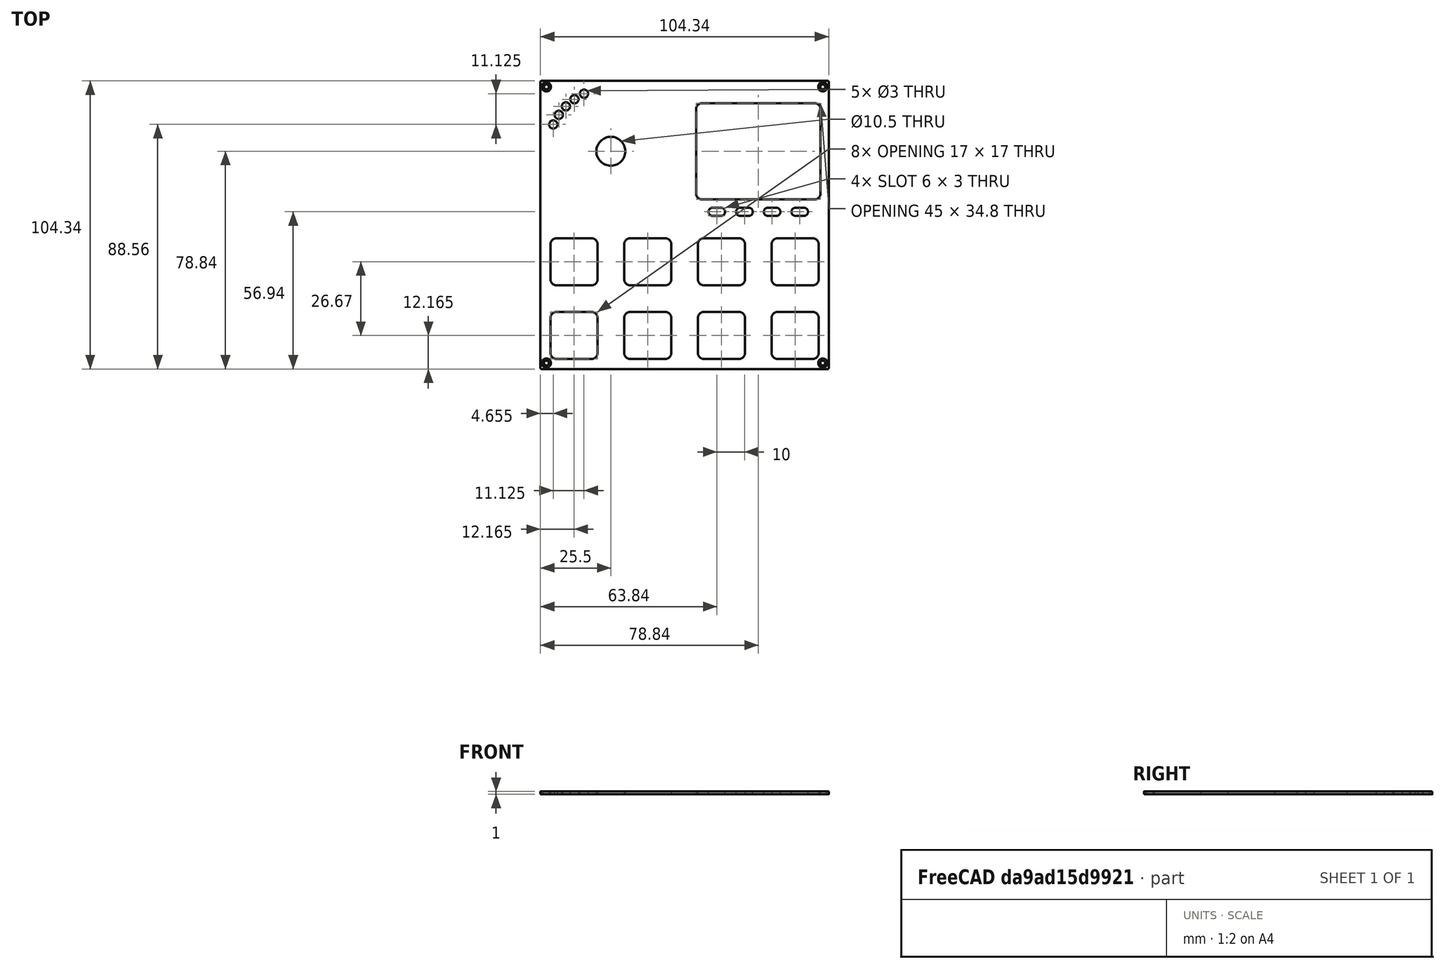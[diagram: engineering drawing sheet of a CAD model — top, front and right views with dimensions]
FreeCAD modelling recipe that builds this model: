
FCSTD DOCUMENT  (FreeCAD 0.21R33771 (Git))
Label: FRONTPANEL-SHEET-VSN1-R
License: All rights reserved
LicenseURL: https://en.wikipedia.org/wiki/All_rights_reserved
objects: TechDraw::DrawViewDimension×16, TechDraw::DrawViewBalloon×13, Sketcher::SketchObject×11, TechDraw::DrawHatch×8, PartDesign::Pocket×5, TechDraw::DrawViewPart×5, TechDraw::DrawViewAnnotation×4, TechDraw::DrawSVGTemplate×2, PartDesign::Body×2, TechDraw::DrawPage×2, Spreadsheet::Sheet×1, PartDesign::Pad×1, PartDesign::Hole×1, PartDesign::FeatureBase×1, TechDraw::DrawComplexSection×1
note: 52 computed .brp shape members not serialized (recipe doc carries the construction recipe); baked Part::Feature solids carry a one-line shape summary decoded from their .brp

FEATURE [TechDraw::DrawSVGTemplate] Template
  EditableTexts = COLOR=Anodized matte black - RAL code: 9004; CreationDate=2024/08/29; E.G.APPROVED=PRELIMINARY; FC-Scale=1:1; FC-Title=VSN1-R - frontpanel; IntechStudioLtd.=Intech Studio Ltd.; MATERIAL=Aluminum 5052-H32; REV=01; STANDARD=ISO 2768 - m
  Height = 297
  Orientation = 1
  Template = <userpath>/Desktop/A3_LandscapeTD_MODIFIED.svg
  Width = 420
FEATURE [Spreadsheet::Sheet] Spreadsheet  label="dim"
  cells = A1='panel_length; B1(panel_length)=104.35; A2='panel_thickness; B2(panel_thickness)=1; A3='panel_radius; B3(panel_radius)==(104.35 - 103.6) / 2; A5='corner_drill_dist; B5(corner_drill_dist)=100; A6='corner_drill_dia; B6(corner_drill_dia)=1.75; A7='corner_drill_countersink; B7(corner_drill_countersink)=3.3; A9='undercut_width; B9(undercut_width)=1; A10='undercut_length; B10(undercut_length)=90; A11='undercut_offset; B11(undercut_offset)=1; A12='undercut_depth; B12(undercut_depth)=0.8; A14='ui_raster; B14(ui_raster)=26.67; A16='light_drill_dia; B16(light_drill_dia)=3; D16='old 2.9; A17='light_bore_dia; B17(light_bore_dia)=3.45; C17='check; D17='old 3.30; E17='DEPRICATED; A18='light_bore_depth; B18(light_bore_depth)=0.4; C18='check; D18='old 0.40; E18='DEPRICATED; A20='pot_drill_dia; B20(pot_drill_dia)=9.8; C20='check; D20='old 6.20; A21='pot_led_dist; B21(pot_led_dist)=8.5; B22=0; A23='but_drill_dia; B23(but_drill_dia)=9.8; A24='but_led_dist; B24(but_led_dist)=8.5; A26='fad_cutout_width; B26(fad_cutout_width)=2.1; C26='check; D26='old 1.50; A27='fad_cutout_length; B27(fad_cutout_length)=36; A28='fad_led_dist; B28(fad_led_dist)=25; A30='enc_drill_dia; B30(enc_drill_dia)=9.8; C30='check; D30='old 6.20; A31='enc_led_dist; B31(enc_led_dist)=8.5; A33='longfad_cutout_width; B33(longfad_cutout_width)=2.1; A34='longfad_cutout_length; B34(longfad_cutout_length)=66; A36='panel_chamfer; B36(panel_chamfer)=0.2; C36='UPDATE DRAWING
FEATURE [Sketcher::SketchObject] Sketch025
  FullyConstrained = true
  MapMode = 5
  Support = -> [XY_Plane011]
  expr: Constraints[49] = <<dim>>.light_drill_dia
  sketch-geometry (28):
    g0: Circle CenterX=-26.67 CenterY=26.67 CenterZ=0 NormalX=0 NormalY=0 NormalZ=1 AngleXU=0 Radius=5.25
    g1: Circle CenterX=26.67 CenterY=26.67 CenterZ=0 NormalX=0 NormalY=0 NormalZ=1 AngleXU=0 Radius=5.25
    g2: LineSegment StartX=-26.67 StartY=26.67 StartZ=0 EndX=0 EndY=26.67 EndZ=0
    g3: LineSegment StartX=0 StartY=26.67 StartZ=0 EndX=0 EndY=0 EndZ=0
    g4: LineSegment StartX=26.67 StartY=26.67 StartZ=0 EndX=0 EndY=26.67 EndZ=0
    g5: Circle CenterX=-26.67 CenterY=26.67 CenterZ=0 NormalX=0 NormalY=0 NormalZ=1 AngleXU=0 Radius=23
    g6: Circle CenterX=26.67 CenterY=26.67 CenterZ=0 NormalX=0 NormalY=0 NormalZ=1 AngleXU=0 Radius=23
    g7: Circle CenterX=-47.5151 CenterY=36.3902 CenterZ=0 NormalX=0 NormalY=0 NormalZ=1 AngleXU=0 Radius=1.5
    g8: Circle CenterX=-45.5105 CenterY=39.8623 CenterZ=0 NormalX=0 NormalY=0 NormalZ=1 AngleXU=0 Radius=1.5
    g9: Circle CenterX=-42.9335 CenterY=42.9335 CenterZ=0 NormalX=0 NormalY=0 NormalZ=1 AngleXU=0 Radius=1.5
    g10: Circle CenterX=-39.8623 CenterY=45.5105 CenterZ=0 NormalX=0 NormalY=0 NormalZ=1 AngleXU=0 Radius=1.5
    g11: Circle CenterX=-36.3902 CenterY=47.5151 CenterZ=0 NormalX=0 NormalY=0 NormalZ=1 AngleXU=0 Radius=1.5
    g12: Circle CenterX=5.82492 CenterY=36.3902 CenterZ=0 NormalX=0 NormalY=0 NormalZ=1 AngleXU=0 Radius=1.5
    g13: Circle CenterX=7.8295 CenterY=39.8623 CenterZ=0 NormalX=0 NormalY=0 NormalZ=1 AngleXU=0 Radius=1.5
    g14: Circle CenterX=10.4065 CenterY=42.9335 CenterZ=0 NormalX=0 NormalY=0 NormalZ=1 AngleXU=0 Radius=1.5
    g15: Circle CenterX=13.4777 CenterY=45.5105 CenterZ=0 NormalX=0 NormalY=0 NormalZ=1 AngleXU=0 Radius=1.5
    g16: Circle CenterX=16.9498 CenterY=47.5151 CenterZ=0 NormalX=0 NormalY=0 NormalZ=1 AngleXU=0 Radius=1.5
    g17: LineSegment StartX=-47.5151 StartY=36.3902 StartZ=0 EndX=5.82492 EndY=36.3902 EndZ=0
    g18: LineSegment StartX=-45.5105 StartY=39.8623 StartZ=0 EndX=7.8295 EndY=39.8623 EndZ=0
    g19: LineSegment StartX=-42.9335 StartY=42.9335 StartZ=0 EndX=10.4065 EndY=42.9335 EndZ=0
    g20: LineSegment StartX=-39.8623 StartY=45.5105 StartZ=0 EndX=13.4777 EndY=45.5105 EndZ=0
    g21: LineSegment StartX=-36.3902 StartY=47.5151 StartZ=0 EndX=16.9498 EndY=47.5151 EndZ=0
    g22: LineSegment StartX=5.82492 StartY=36.3902 StartZ=0 EndX=26.67 EndY=26.67 EndZ=0
    g23: LineSegment StartX=16.9498 StartY=47.5151 StartZ=0 EndX=26.67 EndY=26.67 EndZ=0
    g24: LineSegment StartX=5.82492 StartY=36.3902 StartZ=0 EndX=7.8295 EndY=39.8623 EndZ=0
    g25: LineSegment StartX=7.8295 StartY=39.8623 StartZ=0 EndX=10.4065 EndY=42.9335 EndZ=0
    g26: LineSegment StartX=13.4777 StartY=45.5105 StartZ=0 EndX=10.4065 EndY=42.9335 EndZ=0
    g27: LineSegment StartX=16.9498 StartY=47.5151 StartZ=0 EndX=13.4777 EndY=45.5105 EndZ=0
  constraints (69):
    c: Coincident(g2,g0)
    c: PointOnObject(g2,g-2)
    c: Coincident(g2,g3)
    c: Coincident(g3,g-1)
    c: Coincident(g4,g1)
    c: Coincident(g4,g2)
    c: Equal(g3,g2)
    c: Equal(g2,g4)
    c: Horizontal(g2)
    c: Horizontal(g4)
    c: DistanceY(g3,g3) = 26.67
    c: Equal(g0,g1)
    c: Coincident(g5,g0)
    c: Coincident(g6,g1)
    c: Equal(g6,g5)
    c: PointOnObject(g7,g5)
    c: PointOnObject(g8,g5)
    c: PointOnObject(g9,g5)
    c: PointOnObject(g10,g5)
    c: PointOnObject(g11,g5)
    c: PointOnObject(g12,g6)
    c: PointOnObject(g13,g6)
    c: PointOnObject(g14,g6)
    c: PointOnObject(g15,g6)
    c: PointOnObject(g16,g6)
    c: Equal(g7,g8)
    c: Equal(g8,g9)
    c: Equal(g9,g10)
    c: Equal(g10,g11)
    c: Equal(g11,g12)
    c: Equal(g12,g13)
    c: Equal(g13,g14)
    c: Equal(g14,g15)
    c: Equal(g15,g16)
    c: Coincident(g17,g7)
    c: Coincident(g17,g12)
    c: Coincident(g18,g8)
    c: Coincident(g18,g13)
    c: Horizontal(g18)
    c: Coincident(g19,g9)
    c: Coincident(g19,g14)
    c: Horizontal(g19)
    c: Coincident(g20,g10)
    c: Coincident(g20,g15)
    c: Horizontal(g20)
    c: Coincident(g21,g11)
    c: Horizontal(g21)
    c: Coincident(g21,g16)
    c: Horizontal(g17)
    c: Diameter(g12) = 3
    c: Coincident(g22,g12)
    c: Coincident(g22,g1)
    c: Coincident(g23,g16)
    c: Coincident(g23,g1)
    c: Angle(g22,g4) = 0.436332
    c: Angle(g-2,g23) = 0.436332
    c: Coincident(g24,g12)
    c: Coincident(g24,g13)
    c: Coincident(g25,g13)
    c: Coincident(g26,g15)
    c: Coincident(g26,g25)
    c: Coincident(g27,g16)
    c: Coincident(g27,g15)
    c: Coincident(g25,g14)
    c: Equal(g24,g25)
    c: Equal(g25,g26)
    c: Equal(g26,g27)
    c: Radius(g6) = 23
    c: Diameter(g1) = 10.5
FEATURE [Sketcher::SketchObject] Sketch024  label="TEK2_ButtonLight"
  FullyConstrained = true
  MapMode = 5
  Support = -> [XY_Plane011]
  expr: Constraints[42] = <<dim>>.but_led_dist
  sketch-geometry (17):
    g0: Circle CenterX=-40.005 CenterY=-4.835 CenterZ=0 NormalX=0 NormalY=0 NormalZ=1 AngleXU=0 Radius=2
    g1: Circle CenterX=-13.335 CenterY=-4.835 CenterZ=0 NormalX=0 NormalY=0 NormalZ=1 AngleXU=0 Radius=2
    g2: LineSegment StartX=-40.005 StartY=-4.835 StartZ=0 EndX=-13.335 EndY=-4.835 EndZ=0
    g3: Circle CenterX=13.335 CenterY=-4.835 CenterZ=0 NormalX=0 NormalY=0 NormalZ=1 AngleXU=0 Radius=2
    g4: LineSegment StartX=-13.335 StartY=-4.835 StartZ=0 EndX=13.335 EndY=-4.835 EndZ=0
    g5: Circle CenterX=40.005 CenterY=-4.835 CenterZ=0 NormalX=0 NormalY=0 NormalZ=1 AngleXU=0 Radius=2
    g6: LineSegment StartX=13.335 StartY=-4.835 StartZ=0 EndX=40.005 EndY=-4.835 EndZ=0
    g7: Circle CenterX=-40.005 CenterY=-31.505 CenterZ=0 NormalX=0 NormalY=0 NormalZ=1 AngleXU=0 Radius=2
    g8: LineSegment StartX=-40.005 StartY=-4.835 StartZ=0 EndX=-40.005 EndY=-31.505 EndZ=0
    g9: Circle CenterX=-13.335 CenterY=-31.505 CenterZ=0 NormalX=0 NormalY=0 NormalZ=1 AngleXU=0 Radius=2
    g10: LineSegment StartX=-40.005 StartY=-31.505 StartZ=0 EndX=-13.335 EndY=-31.505 EndZ=0
    g11: Circle CenterX=13.335 CenterY=-31.505 CenterZ=0 NormalX=0 NormalY=0 NormalZ=1 AngleXU=0 Radius=2
    g12: LineSegment StartX=-13.335 StartY=-31.505 StartZ=0 EndX=13.335 EndY=-31.505 EndZ=0
    g13: Circle CenterX=40.005 CenterY=-31.505 CenterZ=0 NormalX=0 NormalY=0 NormalZ=1 AngleXU=0 Radius=2
    g14: LineSegment StartX=13.335 StartY=-31.505 StartZ=0 EndX=40.005 EndY=-31.505 EndZ=0
    g15: LineSegment StartX=-13.335 StartY=-4.835 StartZ=0 EndX=-1.8e-15 EndY=8.5 EndZ=0
    g16: LineSegment StartX=-1.8e-15 StartY=8.5 StartZ=0 EndX=13.335 EndY=-4.835 EndZ=0
  constraints (43):
    c: Diameter(g0) = 4
    c: Coincident(g0,g2)
    c: Coincident(g1,g2)
    c: Coincident(g1,g4)
    c: Coincident(g3,g4)
    c: Coincident(g3,g6)
    c: Coincident(g5,g6)
    c: Coincident(g0,g8)
    c: Coincident(g7,g8)
    c: Coincident(g7,g10)
    c: Coincident(g9,g10)
    c: Coincident(g9,g12)
    c: Coincident(g11,g12)
    c: Coincident(g11,g14)
    c: Coincident(g13,g14)
    c: Horizontal(g4)
    c: Horizontal(g2)
    c: Horizontal(g6)
    c: Horizontal(g10)
    c: Horizontal(g12)
    c: Horizontal(g14)
    c: Vertical(g8)
    c: Equal(g8,g2)
    c: Equal(g2,g10)
    c: Equal(g10,g12)
    c: Equal(g12,g4)
    c: Equal(g4,g6)
    c: Equal(g6,g14)
    c: DistanceX(g4,g4) = 26.67
    c: Equal(g7,g9)
    c: Equal(g9,g11)
    c: Equal(g11,g13)
    c: Equal(g13,g5)
    c: Equal(g5,g3)
    c: Equal(g3,g1)
    c: Equal(g1,g0)
    c: Coincident(g15,g1)
    c: PointOnObject(g15,g-2)
    c: Coincident(g15,g16)
    c: Coincident(g16,g3)
    c: Equal(g16,g15)
    c: Perpendicular(g15,g16)
    c: DistanceY(g-1,g15) = 8.5
FEATURE [Sketcher::SketchObject] Sketch023  label="TEK2_ButtonHole"
  FullyConstrained = true
  MapMode = 5
  Support = -> [XY_Plane011]
  sketch-geometry (17):
    g0: Circle CenterX=-40.005 CenterY=-13.335 CenterZ=0 NormalX=0 NormalY=0 NormalZ=1 AngleXU=0 Radius=2
    g1: Circle CenterX=-13.335 CenterY=-13.335 CenterZ=0 NormalX=0 NormalY=0 NormalZ=1 AngleXU=0 Radius=2
    g2: LineSegment StartX=-40.005 StartY=-13.335 StartZ=0 EndX=-13.335 EndY=-13.335 EndZ=0
    g3: Circle CenterX=13.335 CenterY=-13.335 CenterZ=0 NormalX=0 NormalY=0 NormalZ=1 AngleXU=0 Radius=2
    g4: LineSegment StartX=-13.335 StartY=-13.335 StartZ=0 EndX=13.335 EndY=-13.335 EndZ=0
    g5: Circle CenterX=40.005 CenterY=-13.335 CenterZ=0 NormalX=0 NormalY=0 NormalZ=1 AngleXU=0 Radius=2
    g6: LineSegment StartX=13.335 StartY=-13.335 StartZ=0 EndX=40.005 EndY=-13.335 EndZ=0
    g7: Circle CenterX=-40.005 CenterY=-40.005 CenterZ=0 NormalX=0 NormalY=0 NormalZ=1 AngleXU=0 Radius=2
    g8: LineSegment StartX=-40.005 StartY=-13.335 StartZ=0 EndX=-40.005 EndY=-40.005 EndZ=0
    g9: Circle CenterX=-13.335 CenterY=-40.005 CenterZ=0 NormalX=0 NormalY=0 NormalZ=1 AngleXU=0 Radius=2
    g10: LineSegment StartX=-40.005 StartY=-40.005 StartZ=0 EndX=-13.335 EndY=-40.005 EndZ=0
    g11: Circle CenterX=13.335 CenterY=-40.005 CenterZ=0 NormalX=0 NormalY=0 NormalZ=1 AngleXU=0 Radius=2
    g12: LineSegment StartX=-13.335 StartY=-40.005 StartZ=0 EndX=13.335 EndY=-40.005 EndZ=0
    g13: Circle CenterX=40.005 CenterY=-40.005 CenterZ=0 NormalX=0 NormalY=0 NormalZ=1 AngleXU=0 Radius=2
    g14: LineSegment StartX=13.335 StartY=-40.005 StartZ=0 EndX=40.005 EndY=-40.005 EndZ=0
    g15: LineSegment StartX=0 StartY=0 StartZ=0 EndX=13.335 EndY=-13.335 EndZ=0
    g16: LineSegment StartX=0 StartY=0 StartZ=0 EndX=-13.335 EndY=-13.335 EndZ=0
  constraints (42):
    c: Diameter(g0) = 4
    c: Coincident(g0,g2)
    c: Coincident(g1,g2)
    c: Coincident(g1,g4)
    c: Coincident(g3,g4)
    c: Coincident(g3,g6)
    c: Coincident(g5,g6)
    c: Coincident(g0,g8)
    c: Coincident(g7,g8)
    c: Coincident(g7,g10)
    c: Coincident(g9,g10)
    c: Coincident(g9,g12)
    c: Coincident(g11,g12)
    c: Coincident(g11,g14)
    c: Coincident(g13,g14)
    c: Coincident(g-1,g16)
    c: Coincident(g16,g1)
    c: Coincident(g15,g3)
    c: Horizontal(g4)
    c: Horizontal(g2)
    c: Horizontal(g6)
    c: Horizontal(g10)
    c: Horizontal(g12)
    c: Horizontal(g14)
    c: Vertical(g8)
    c: Equal(g8,g2)
    c: Equal(g2,g10)
    c: Equal(g10,g12)
    c: Equal(g12,g4)
    c: Equal(g4,g6)
    c: Equal(g6,g14)
    c: DistanceX(g4,g4) = 26.67
    c: Equal(g16,g15)
    c: Coincident(g15,g16)
    c: Perpendicular(g15,g16)
    c: Equal(g7,g9)
    c: Equal(g9,g11)
    c: Equal(g11,g13)
    c: Equal(g13,g5)
    c: Equal(g5,g3)
    c: Equal(g3,g1)
    c: Equal(g1,g0)
FEATURE [Sketcher::SketchObject] Sketch001
  FullyConstrained = true
  MapMode = 5
  Support = -> [XY_Plane]
  expr: Constraints[13] = <<dim>>.corner_drill_dist
  sketch-geometry (9):
    g0: LineSegment StartX=-50 StartY=50 StartZ=0 EndX=-50 EndY=-50 EndZ=0
    g1: LineSegment StartX=-50 StartY=-50 StartZ=0 EndX=50 EndY=-50 EndZ=0
    g2: LineSegment StartX=50 StartY=-50 StartZ=0 EndX=50 EndY=50 EndZ=0
    g3: LineSegment StartX=50 StartY=50 StartZ=0 EndX=-50 EndY=50 EndZ=0
    g4: Circle CenterX=0 CenterY=0 CenterZ=0 NormalX=0 NormalY=0 NormalZ=1 AngleXU=0 Radius=70.7107
    g5: Circle CenterX=-50 CenterY=50 CenterZ=0 NormalX=0 NormalY=0 NormalZ=1 AngleXU=0 Radius=0.5
    g6: Circle CenterX=50 CenterY=50 CenterZ=0 NormalX=0 NormalY=0 NormalZ=1 AngleXU=0 Radius=0.5
    g7: Circle CenterX=50 CenterY=-50 CenterZ=0 NormalX=0 NormalY=0 NormalZ=1 AngleXU=0 Radius=0.5
    g8: Circle CenterX=-50 CenterY=-50 CenterZ=0 NormalX=0 NormalY=0 NormalZ=1 AngleXU=0 Radius=0.5
  constraints (22):
    c: Coincident(g0,g1)
    c: Coincident(g1,g2)
    c: Coincident(g2,g3)
    c: Coincident(g3,g0)
    c: Equal(g0,g1)
    c: Equal(g0,g2)
    c: Equal(g0,g3)
    c: PointOnObject(g0,g4)
    c: PointOnObject(g1,g4)
    c: PointOnObject(g2,g4)
    c: PointOnObject(g3,g4)
    c: Coincident(g4,g-1)
    c: Horizontal(g3)
    c: DistanceX(g3,g3) = 100
    c: Coincident(g5,g0)
    c: Coincident(g6,g2)
    c: Coincident(g7,g1)
    c: Coincident(g8,g0)
    c: Diameter(g8) = 1
    c: Equal(g8,g7)
    c: Equal(g8,g6)
    c: Equal(g8,g5)
FEATURE [Sketcher::SketchObject] Sketch002
  AttachmentOffset = pos=(0,0,-4.8) rot=(0,0,1;0rad)
  FullyConstrained = true
  MapMode = 5
  Placement = pos=(0,0,-4.8) rot=(0,0,1;0rad)
  Support = -> [XY_Plane]
  expr: .AttachmentOffset.Base.z = -<<dim>>.undercut_depth - 4
  expr: Constraints[91] = <<dim>>.undercut_length
  expr: Constraints[92] = <<dim>>.undercut_width
  expr: Constraints[93] = <<dim>>.panel_length / 2 - <<dim>>.undercut_offset - <<dim>>.undercut_width / 2
  sketch-geometry (40):
    g0: LineSegment StartX=-45 StartY=50.175 StartZ=0 EndX=45 EndY=50.175 EndZ=0
    g1: LineSegment StartX=-45 StartY=51.175 StartZ=0 EndX=45 EndY=51.175 EndZ=0
    g2: LineSegment StartX=-50.675 StartY=45 StartZ=0 EndX=0 EndY=0 EndZ=0
    g3: LineSegment StartX=0 StartY=0 StartZ=0 EndX=-50.675 EndY=-45 EndZ=0
    g4: LineSegment StartX=0 StartY=0 StartZ=0 EndX=-45 EndY=50.675 EndZ=0
    g5: LineSegment StartX=45 StartY=50.675 StartZ=0 EndX=0 EndY=0 EndZ=0
    g6: LineSegment StartX=0 StartY=0 StartZ=0 EndX=50.675 EndY=45 EndZ=0
    g7: LineSegment StartX=50.675 StartY=-45 StartZ=0 EndX=0 EndY=0 EndZ=0
    g8: LineSegment StartX=0 StartY=0 StartZ=0 EndX=45 EndY=-50.675 EndZ=0
    g9: LineSegment StartX=0 StartY=0 StartZ=0 EndX=-45 EndY=-50.675 EndZ=0
    g10: ArcOfCircle CenterX=45 CenterY=50.675 CenterZ=0 NormalX=0 NormalY=0 NormalZ=1 AngleXU=0 Radius=0.5 StartAngle=4.71239 EndAngle=6.28319
    g11: ArcOfCircle CenterX=45 CenterY=50.675 CenterZ=0 NormalX=0 NormalY=0 NormalZ=1 AngleXU=0 Radius=0.5 StartAngle=0 EndAngle=1.5708
    g12: LineSegment StartX=45 StartY=50.675 StartZ=0 EndX=45.5 EndY=50.675 EndZ=0
    g13: ArcOfCircle CenterX=-45 CenterY=50.675 CenterZ=0 NormalX=0 NormalY=0 NormalZ=1 AngleXU=0 Radius=0.5 StartAngle=3.14159 EndAngle=4.71239
    g14: ArcOfCircle CenterX=-45 CenterY=50.675 CenterZ=0 NormalX=0 NormalY=0 NormalZ=1 AngleXU=0 Radius=0.5 StartAngle=1.5708 EndAngle=3.14159
    g15: LineSegment StartX=-45.5 StartY=50.675 StartZ=0 EndX=-45 EndY=50.675 EndZ=0
    g16: LineSegment StartX=-45 StartY=-51.175 StartZ=0 EndX=45 EndY=-51.175 EndZ=0
    g17: LineSegment StartX=-45 StartY=-50.175 StartZ=0 EndX=45 EndY=-50.175 EndZ=0
    g18: ArcOfCircle CenterX=45 CenterY=-50.675 CenterZ=0 NormalX=0 NormalY=0 NormalZ=1 AngleXU=0 Radius=0.5 StartAngle=4.71239 EndAngle=6.28319
    g19: ArcOfCircle CenterX=45 CenterY=-50.675 CenterZ=0 NormalX=0 NormalY=0 NormalZ=1 AngleXU=0 Radius=0.5 StartAngle=0 EndAngle=1.5708
    g20: LineSegment StartX=45 StartY=-50.675 StartZ=0 EndX=45.5 EndY=-50.675 EndZ=0
    g21: ArcOfCircle CenterX=-45 CenterY=-50.675 CenterZ=0 NormalX=0 NormalY=0 NormalZ=1 AngleXU=0 Radius=0.5 StartAngle=3.14159 EndAngle=4.71239
    g22: ArcOfCircle CenterX=-45 CenterY=-50.675 CenterZ=0 NormalX=0 NormalY=0 NormalZ=1 AngleXU=0 Radius=0.5 StartAngle=1.5708 EndAngle=3.14159
    g23: LineSegment StartX=-45.5 StartY=-50.675 StartZ=0 EndX=-45 EndY=-50.675 EndZ=0
    g24: LineSegment StartX=51.175 StartY=-45 StartZ=0 EndX=51.175 EndY=45 EndZ=0
    g25: LineSegment StartX=50.175 StartY=-45 StartZ=0 EndX=50.175 EndY=45 EndZ=0
    g26: ArcOfCircle CenterX=50.675 CenterY=45 CenterZ=0 NormalX=0 NormalY=0 NormalZ=1 AngleXU=0 Radius=0.5 StartAngle=3.8e-15 EndAngle=1.5708
    g27: ArcOfCircle CenterX=50.675 CenterY=45 CenterZ=0 NormalX=0 NormalY=0 NormalZ=1 AngleXU=0 Radius=0.5 StartAngle=1.5708 EndAngle=3.14159
    g28: LineSegment StartX=50.675 StartY=45 StartZ=0 EndX=50.675 EndY=45.5 EndZ=0
    g29: ArcOfCircle CenterX=50.675 CenterY=-45 CenterZ=0 NormalX=0 NormalY=0 NormalZ=1 AngleXU=0 Radius=0.5 StartAngle=4.71239 EndAngle=6.28319
    g30: ArcOfCircle CenterX=50.675 CenterY=-45 CenterZ=0 NormalX=0 NormalY=0 NormalZ=1 AngleXU=0 Radius=0.5 StartAngle=3.14159 EndAngle=4.71239
    g31: LineSegment StartX=50.675 StartY=-45.5 StartZ=0 EndX=50.675 EndY=-45 EndZ=0
    g32: LineSegment StartX=-50.175 StartY=-45 StartZ=0 EndX=-50.175 EndY=45 EndZ=0
    g33: LineSegment StartX=-51.175 StartY=-45 StartZ=0 EndX=-51.175 EndY=45 EndZ=0
    g34: ArcOfCircle CenterX=-50.675 CenterY=45 CenterZ=0 NormalX=0 NormalY=0 NormalZ=1 AngleXU=0 Radius=0.5 StartAngle=1.4e-15 EndAngle=1.5708
    g35: ArcOfCircle CenterX=-50.675 CenterY=45 CenterZ=0 NormalX=0 NormalY=0 NormalZ=1 AngleXU=0 Radius=0.5 StartAngle=1.5708 EndAngle=3.14159
    g36: LineSegment StartX=-50.675 StartY=45 StartZ=0 EndX=-50.675 EndY=45.5 EndZ=0
    g37: ArcOfCircle CenterX=-50.675 CenterY=-45 CenterZ=0 NormalX=0 NormalY=0 NormalZ=1 AngleXU=0 Radius=0.5 StartAngle=4.71239 EndAngle=6.28319
    g38: ArcOfCircle CenterX=-50.675 CenterY=-45 CenterZ=0 NormalX=0 NormalY=0 NormalZ=1 AngleXU=0 Radius=0.5 StartAngle=3.14159 EndAngle=4.71239
    g39: LineSegment StartX=-50.675 StartY=-45.5 StartZ=0 EndX=-50.675 EndY=-45 EndZ=0
  constraints (96):
    c: Horizontal(g0)
    c: Coincident(g2,g-1)
    c: Coincident(g2,g3)
    c: Coincident(g-1,g4)
    c: Coincident(g5,g-1)
    c: Coincident(g5,g6)
    c: Coincident(g7,g-1)
    c: Coincident(g7,g8)
    c: Coincident(g-1,g9)
    c: Equal(g5,g6)
    c: Equal(g6,g8)
    c: Equal(g8,g7)
    c: Equal(g7,g9)
    c: Equal(g9,g3)
    c: Equal(g3,g2)
    c: Equal(g2,g4)
    c: Coincident(g10,g5)
    c: Coincident(g11,g10)
    c: Coincident(g11,g10)
    c: Tangent(g11,g1) = 1.5708
    c: Tangent(g10,g0) = -1.5708
    c: Coincident(g12,g10)
    c: Coincident(g12,g10)
    c: Horizontal(g12)
    c: Coincident(g13,g4)
    c: Coincident(g14,g13)
    c: Coincident(g14,g13)
    c: Tangent(g14,g1) = 1.5708
    c: Tangent(g13,g0) = -1.5708
    c: Coincident(g15,g13)
    c: Coincident(g15,g13)
    c: Horizontal(g15)
    c: Horizontal(g1)
    c: Horizontal(g16)
    c: Coincident(g19,g18)
    c: Coincident(g19,g18)
    c: Tangent(g19,g17) = 1.5708
    c: Tangent(g18,g16) = -1.5708
    c: Coincident(g20,g18)
    c: Coincident(g20,g18)
    c: Horizontal(g20)
    c: Coincident(g22,g21)
    c: Coincident(g22,g21)
    c: Tangent(g22,g17) = 1.5708
    c: Tangent(g21,g16) = -1.5708
    c: Coincident(g23,g21)
    c: Coincident(g23,g21)
    c: Horizontal(g23)
    c: Horizontal(g17)
    c: Coincident(g21,g9)
    c: Coincident(g8,g18)
    c: Equal(g22,g14)
    c: Equal(g17,g1)
    c: Coincident(g27,g26)
    c: Coincident(g27,g26)
    c: Tangent(g27,g25) = 1.5708
    c: Tangent(g26,g24) = -1.5708
    c: Coincident(g28,g26)
    c: Coincident(g28,g26)
    c: Coincident(g30,g29)
    c: Coincident(g30,g29)
    c: Tangent(g30,g25) = 1.5708
    c: Tangent(g29,g24) = -1.5708
    c: Coincident(g31,g29)
    c: Coincident(g31,g29)
    c: Vertical(g31)
    c: Vertical(g28)
    c: Vertical(g25)
    c: Vertical(g24)
    c: Coincident(g35,g34)
    c: Coincident(g35,g34)
    c: Tangent(g35,g33) = 1.5708
    c: Tangent(g34,g32) = -1.5708
    c: Coincident(g36,g34)
    c: Coincident(g36,g34)
    c: Coincident(g38,g37)
    c: Coincident(g38,g37)
    c: Tangent(g38,g33) = 1.5708
    c: Tangent(g37,g32) = -1.5708
    c: Coincident(g39,g37)
    c: Coincident(g39,g37)
    c: Vertical(g39)
    c: Vertical(g36)
    c: Vertical(g33)
    c: Vertical(g32)
    c: Coincident(g6,g26)
    c: Coincident(g7,g29)
    c: Equal(g25,g0)
    c: Equal(g11,g27)
    c: Equal(g1,g33)
    c: Equal(g35,g11)
    c: DistanceX(g13,g10) = 90
    c: Diameter(g13) = 1
    c: DistanceY(g-1,g13) = 50.675
    c: Coincident(g2,g34)
    c: Coincident(g3,g37)
FEATURE [Sketcher::SketchObject] Sketch
  FullyConstrained = true
  MapMode = 5
  Support = -> [XY_Plane]
  expr: Constraints[12] = <<dim>>.panel_radius
  expr: Constraints[16] = <<dim>>.panel_length
  sketch-geometry (11):
    g0: LineSegment StartX=-51.8 StartY=52.175 StartZ=0 EndX=51.8 EndY=52.175 EndZ=0
    g1: LineSegment StartX=52.175 StartY=51.8 StartZ=0 EndX=52.175 EndY=-51.8 EndZ=0
    g2: LineSegment StartX=51.8 StartY=-52.175 StartZ=0 EndX=-51.8 EndY=-52.175 EndZ=0
    g3: LineSegment StartX=-52.175 StartY=-51.8 StartZ=0 EndX=-52.175 EndY=51.8 EndZ=0
    g4: ArcOfCircle CenterX=-51.8 CenterY=51.8 CenterZ=0 NormalX=0 NormalY=0 NormalZ=1 AngleXU=0 Radius=0.375 StartAngle=1.5708 EndAngle=3.14159
    g5: ArcOfCircle CenterX=51.8 CenterY=51.8 CenterZ=0 NormalX=0 NormalY=0 NormalZ=1 AngleXU=0 Radius=0.375 StartAngle=8.4e-15 EndAngle=1.5708
    g6: ArcOfCircle CenterX=51.8 CenterY=-51.8 CenterZ=0 NormalX=0 NormalY=0 NormalZ=1 AngleXU=0 Radius=0.375 StartAngle=4.71239 EndAngle=6.28319
    g7: ArcOfCircle CenterX=-51.8 CenterY=-51.8 CenterZ=0 NormalX=0 NormalY=0 NormalZ=1 AngleXU=0 Radius=0.375 StartAngle=3.14159 EndAngle=4.71239
    g8: LineSegment StartX=-51.8 StartY=51.8 StartZ=0 EndX=0 EndY=0 EndZ=0
    g9: LineSegment StartX=0 StartY=0 StartZ=0 EndX=51.8 EndY=51.8 EndZ=0
    g10: LineSegment StartX=0 StartY=0 StartZ=0 EndX=-51.8 EndY=-51.8 EndZ=0
  constraints (26):
    c: Horizontal(g0)
    c: Horizontal(g2)
    c: Vertical(g1)
    c: Vertical(g3)
    c: Tangent(g3,g4) = 1.5708
    c: Tangent(g0,g4) = 1.5708
    c: Tangent(g0,g5) = 1.5708
    c: Tangent(g1,g5) = 1.5708
    c: Tangent(g1,g6) = 1.5708
    c: Tangent(g2,g6) = 1.5708
    c: Tangent(g2,g7) = 1.5708
    c: Tangent(g3,g7) = 1.5708
    c: Radius(g4) = 0.375
    c: Equal(g4,g5)
    c: Equal(g4,g6)
    c: Equal(g4,g7)
    c: DistanceX(g3,g1) = 104.35
    c: Equal(g3,g0)
    c: Coincident(g8,g4)
    c: Coincident(g8,g-1)
    c: Coincident(g8,g9)
    c: Coincident(g9,g5)
    c: Coincident(g-1,g10)
    c: Coincident(g10,g7)
    c: Equal(g10,g8)
    c: Equal(g8,g9)
FEATURE [PartDesign::Pad] Pad  label="panel"
  AllowMultiFace = false
  Direction = (0,0,1)
  Length = 1
  Length2 = 100
  Profile = -> Sketch
  Reversed = true
  Type = 0
  expr: Length = <<dim>>.panel_thickness
FEATURE [PartDesign::Pocket] Pocket
  AllowMultiFace = false
  BaseFeature = -> Pad
  Direction = (0,0,-1)
  Length = 5
  Length2 = 100
  Profile = -> Sketch002
  Type = 1
FEATURE [PartDesign::Hole] Hole
  BaseFeature = -> Pocket
  CustomThreadClearance = 0
  Depth = 298.105
  DepthType = 1
  Diameter = 1.75
  DrillForDepth = false
  DrillPoint = 1
  DrillPointAngle = 118
  HoleCutCountersinkAngle = 90
  HoleCutCustomValues = false
  HoleCutDepth = 0
  HoleCutDiameter = 3.3
  HoleCutType = 2
  ModelThread = false
  Profile = -> Sketch001
  Tapered = false
  TaperedAngle = 90
  ThreadClass = 0
  ThreadDepth = 298.105
  ThreadDepthType = 0
  ThreadDirection = 0
  ThreadFit = 0
  ThreadSize = 0
  ThreadType = 0
  Threaded = false
  UseCustomThreadClearance = false
  expr: Diameter = <<dim>>.corner_drill_dia
  expr: HoleCutDiameter = <<dim>>.corner_drill_countersink
FEATURE [PartDesign::Body] Body  label="Base"
  Group = -> [Sketch,Pad,Sketch001,Sketch002,Pocket,Hole]
  Origin = -> Origin
  Tip = -> Hole
FEATURE [PartDesign::FeatureBase] Clone009
  BaseFeature = -> Body
FEATURE [PartDesign::Pocket] Pocket007  label="TEK2_TEK_Light"
  BaseFeature = -> Clone009
  Direction = (0,0,-1)
  Length = 5
  Length2 = 5
  Profile = -> Sketch025
  ReferenceAxis = -> Sketch025 [N_Axis]
  Type = 0
FEATURE [Sketcher::SketchObject] Sketch026  label="Section A-A"
  FullyConstrained = false
  MapMode = 5
  Support = -> [XY_Plane011]
  sketch-geometry (1):
    g0: LineSegment StartX=-53.5 StartY=-50 StartZ=0 EndX=-46.5 EndY=-50 EndZ=0
  constraints (2):
    c: Horizontal(g0)
    c: DistanceX(g0,g0) = 7
FEATURE [TechDraw::DrawViewAnnotation] Annotation
  Font = osifont
  LineSpace = 100
  LockPosition = false
  MaxWidth = -1
  Rotation = 0
  ScaleType = 0
  Text = 10:1
  TextSize = 4
  TextStyle = 0
  X = 298.164
  Y = 82.211
FEATURE [TechDraw::DrawViewAnnotation] Annotation001
  Font = osifont
  LineSpace = 100
  LockPosition = false
  MaxWidth = -1
  Rotation = 0
  ScaleType = 0
  Text = 1:2
  TextSize = 4
  TextStyle = 0
  X = 186.806
  Y = 53.0158
FEATURE [Sketcher::SketchObject] Sketch027
  FullyConstrained = true
  MapMode = 5
  Support = -> [XY_Plane011]
  sketch-geometry (11):
    g0: LineSegment StartX=4.17 StartY=11.27 StartZ=0 EndX=4.17 EndY=42.07 EndZ=0
    g1: LineSegment StartX=6.17 StartY=44.07 StartZ=0 EndX=47.17 EndY=44.07 EndZ=0
    g2: LineSegment StartX=49.17 StartY=42.07 StartZ=0 EndX=49.17 EndY=11.27 EndZ=0
    g3: LineSegment StartX=47.17 StartY=9.27 StartZ=0 EndX=6.17 EndY=9.27 EndZ=0
    g4: GeomPoint X=26.67 Y=26.67 Z=0
    g5: ArcOfCircle CenterX=6.17 CenterY=42.07 CenterZ=0 NormalX=0 NormalY=0 NormalZ=1 AngleXU=0 Radius=2 StartAngle=1.5708 EndAngle=3.14159
    g6: ArcOfCircle CenterX=47.17 CenterY=42.07 CenterZ=0 NormalX=0 NormalY=0 NormalZ=1 AngleXU=0 Radius=2 StartAngle=-1.8e-15 EndAngle=1.5708
    g7: ArcOfCircle CenterX=47.17 CenterY=11.27 CenterZ=0 NormalX=0 NormalY=0 NormalZ=1 AngleXU=0 Radius=2 StartAngle=4.71239 EndAngle=6.28319
    g8: ArcOfCircle CenterX=6.17 CenterY=11.27 CenterZ=0 NormalX=0 NormalY=0 NormalZ=1 AngleXU=0 Radius=2 StartAngle=3.14159 EndAngle=4.71239
    g9: LineSegment StartX=26.67 StartY=44.07 StartZ=0 EndX=26.67 EndY=9.27 EndZ=0
    g10: LineSegment StartX=4.17 StartY=26.67 StartZ=0 EndX=49.17 EndY=26.67 EndZ=0
  constraints (29):
    c: Horizontal(g1)
    c: Horizontal(g3)
    c: Vertical(g0)
    c: Vertical(g2)
    c: DistanceY(g-1,g4) = 26.67
    c: Tangent(g1,g5) = 1.5708
    c: Tangent(g0,g5) = 1.5708
    c: Tangent(g1,g6) = 1.5708
    c: Tangent(g2,g6) = 1.5708
    c: Tangent(g2,g7) = 1.5708
    c: Tangent(g3,g7) = 1.5708
    c: Tangent(g3,g8) = 1.5708
    c: Tangent(g0,g8) = 1.5708
    c: Equal(g5,g6)
    c: Equal(g6,g7)
    c: Equal(g7,g8)
    c: DistanceX(g0,g2) = 45
    c: DistanceY(g3,g1) = 34.8
    c: PointOnObject(g9,g3)
    c: Vertical(g9)
    c: PointOnObject(g10,g0)
    c: Horizontal(g10)
    c: Symmetric(g2,g2,g10)
    c: Symmetric(g1,g1,g9)
    c: PointOnObject(g4,g9)
    c: PointOnObject(g4,g10)
    c: Diameter(g6) = 4
    c: DistanceX(g4,g-1) = -26.67
    c: DistanceY(g-1,g3) = 9.27
FEATURE [PartDesign::Pocket] Pocket008  label="TEK1_display"
  BaseFeature = -> Pocket007
  Direction = (0,0,-1)
  Length = 5
  Length2 = 5
  Profile = -> Sketch027
  ReferenceAxis = -> Sketch027 [N_Axis]
  Type = 1
FEATURE [Sketcher::SketchObject] Sketch028  label="LocatorPin"
  FullyConstrained = true
  MapMode = 5
  Support = -> [XY_Plane011]
  sketch-geometry (3):
    g0: Circle CenterX=-48.77 CenterY=8.17 CenterZ=0 NormalX=0 NormalY=0 NormalZ=1 AngleXU=0 Radius=0.6
    g1: Circle CenterX=-4.57 CenterY=45.17 CenterZ=0 NormalX=0 NormalY=0 NormalZ=1 AngleXU=0 Radius=0.6
    g2: GeomPoint X=-26.67 Y=26.67 Z=0
  constraints (8):
    c: Equal(g1,g0)
    c: Diameter(g1) = 1.2
    c: DistanceX(g2,g-1) = 26.67
    c: DistanceY(g-1,g2) = 26.67
    c: DistanceX(g0,g2) = 22.1
    c: DistanceY(g0,g2) = 18.5
    c: DistanceX(g2,g1) = 22.1
    c: DistanceY(g2,g1) = 18.5
FEATURE [Sketcher::SketchObject] Sketch029
  FullyConstrained = true
  MapMode = 5
  Support = -> [XY_Plane011]
  sketch-geometry (39):
    g0: LineSegment StartX=6.27 StartY=4.77 StartZ=0 EndX=47.07 EndY=4.77 EndZ=0
    g1: GeomPoint X=26.67 Y=4.77 Z=0
    g2: LineSegment StartX=18.67 StartY=3.12 StartZ=0 EndX=18.67 EndY=6.42 EndZ=0
    g3: LineSegment StartX=18.67 StartY=6.42 StartZ=0 EndX=24.67 EndY=6.42 EndZ=0
    g4: LineSegment StartX=24.67 StartY=6.42 StartZ=0 EndX=24.67 EndY=3.12 EndZ=0
    g5: LineSegment StartX=24.67 StartY=3.12 StartZ=0 EndX=18.67 EndY=3.12 EndZ=0
    g6: GeomPoint X=21.67 Y=4.77 Z=0
    g7: LineSegment StartX=8.67 StartY=3.12 StartZ=0 EndX=8.67 EndY=6.42 EndZ=0
    g8: LineSegment StartX=8.67 StartY=6.42 StartZ=0 EndX=14.67 EndY=6.42 EndZ=0
    g9: LineSegment StartX=14.67 StartY=6.42 StartZ=0 EndX=14.67 EndY=3.12 EndZ=0
    g10: LineSegment StartX=14.67 StartY=3.12 StartZ=0 EndX=8.67 EndY=3.12 EndZ=0
    g11: GeomPoint X=11.67 Y=4.77 Z=0
    g12: LineSegment StartX=28.67 StartY=3.12 StartZ=0 EndX=28.67 EndY=6.42 EndZ=0
    g13: LineSegment StartX=28.67 StartY=6.42 StartZ=0 EndX=34.67 EndY=6.42 EndZ=0
    g14: LineSegment StartX=34.67 StartY=6.42 StartZ=0 EndX=34.67 EndY=3.12 EndZ=0
    g15: LineSegment StartX=34.67 StartY=3.12 StartZ=0 EndX=28.67 EndY=3.12 EndZ=0
    g16: GeomPoint X=31.67 Y=4.77 Z=0
    g17: LineSegment StartX=38.67 StartY=3.12 StartZ=0 EndX=38.67 EndY=6.42 EndZ=0
    g18: LineSegment StartX=38.67 StartY=6.42 StartZ=0 EndX=44.67 EndY=6.42 EndZ=0
    g19: LineSegment StartX=44.67 StartY=6.42 StartZ=0 EndX=44.67 EndY=3.12 EndZ=0
    g20: LineSegment StartX=44.67 StartY=3.12 StartZ=0 EndX=38.67 EndY=3.12 EndZ=0
    g21: GeomPoint X=41.67 Y=4.77 Z=0
    g22: ArcOfCircle CenterX=20.17 CenterY=4.77 CenterZ=0 NormalX=0 NormalY=0 NormalZ=1 AngleXU=0 Radius=1.5 StartAngle=1.5708 EndAngle=4.71239
    g23: ArcOfCircle CenterX=23.17 CenterY=4.77 CenterZ=0 NormalX=0 NormalY=0 NormalZ=1 AngleXU=0 Radius=1.5 StartAngle=4.71239 EndAngle=7.85398
    g24: LineSegment StartX=20.17 StartY=3.27 StartZ=0 EndX=23.17 EndY=3.27 EndZ=0
    g25: LineSegment StartX=23.17 StartY=6.27 StartZ=0 EndX=20.17 EndY=6.27 EndZ=0
    g26: ArcOfCircle CenterX=30.17 CenterY=4.77 CenterZ=0 NormalX=0 NormalY=0 NormalZ=1 AngleXU=0 Radius=1.5 StartAngle=1.5708 EndAngle=4.71239
    g27: ArcOfCircle CenterX=33.17 CenterY=4.77 CenterZ=0 NormalX=0 NormalY=0 NormalZ=1 AngleXU=0 Radius=1.5 StartAngle=4.71239 EndAngle=7.85398
    g28: LineSegment StartX=30.17 StartY=3.27 StartZ=0 EndX=33.17 EndY=3.27 EndZ=0
    g29: LineSegment StartX=33.17 StartY=6.27 StartZ=0 EndX=30.17 EndY=6.27 EndZ=0
    g30: ArcOfCircle CenterX=40.17 CenterY=4.77 CenterZ=0 NormalX=0 NormalY=0 NormalZ=1 AngleXU=0 Radius=1.5 StartAngle=1.5708 EndAngle=4.71239
    g31: ArcOfCircle CenterX=43.17 CenterY=4.77 CenterZ=0 NormalX=0 NormalY=0 NormalZ=1 AngleXU=0 Radius=1.5 StartAngle=4.71239 EndAngle=7.85398
    g32: LineSegment StartX=40.17 StartY=3.27 StartZ=0 EndX=43.17 EndY=3.27 EndZ=0
    g33: LineSegment StartX=43.17 StartY=6.27 StartZ=0 EndX=40.17 EndY=6.27 EndZ=0
    g34: ArcOfCircle CenterX=10.17 CenterY=4.77 CenterZ=0 NormalX=0 NormalY=0 NormalZ=1 AngleXU=0 Radius=1.5 StartAngle=1.5708 EndAngle=4.71239
    g35: ArcOfCircle CenterX=13.17 CenterY=4.77 CenterZ=0 NormalX=0 NormalY=0 NormalZ=1 AngleXU=0 Radius=1.5 StartAngle=4.71239 EndAngle=7.85398
    g36: LineSegment StartX=10.17 StartY=3.27 StartZ=0 EndX=13.17 EndY=3.27 EndZ=0
    g37: LineSegment StartX=13.17 StartY=6.27 StartZ=0 EndX=10.17 EndY=6.27 EndZ=0
    g38: GeomPoint X=26.67 Y=11.37 Z=0
  constraints (94):
    c: Horizontal(g0)
    c: DistanceX(g0,g0) = 40.8
    c: Symmetric(g0,g0,g1)
    c: DistanceX(g1,g-1) = -26.67
    c: Coincident(g2,g3)
    c: Coincident(g3,g4)
    c: Coincident(g4,g5)
    c: Coincident(g5,g2)
    c: Horizontal(g3)
    c: Horizontal(g5)
    c: Vertical(g2)
    c: Vertical(g4)
    c: Symmetric(g3,g2,g6)
    c: PointOnObject(g6,g0)
    c: Coincident(g7,g8)
    c: Coincident(g8,g9)
    c: Coincident(g9,g10)
    c: Coincident(g10,g7)
    c: Horizontal(g8)
    c: Horizontal(g10)
    c: Vertical(g7)
    c: Vertical(g9)
    c: Symmetric(g8,g7,g11)
    c: PointOnObject(g11,g0)
    c: Coincident(g12,g13)
    c: Coincident(g13,g14)
    c: Coincident(g14,g15)
    c: Coincident(g15,g12)
    c: Horizontal(g13)
    c: Horizontal(g15)
    c: Vertical(g12)
    c: Vertical(g14)
    c: Symmetric(g13,g12,g16)
    c: Coincident(g17,g18)
    c: Coincident(g18,g19)
    c: Coincident(g19,g20)
    c: Coincident(g20,g17)
    c: Horizontal(g18)
    c: Horizontal(g20)
    c: Vertical(g17)
    c: Vertical(g19)
    c: Symmetric(g18,g17,g21)
    c: Symmetric(g16,g6,g1)
    c: Symmetric(g11,g21,g1)
    c: Equal(g13,g3)
    c: Equal(g3,g8)
    c: Equal(g8,g18)
    c: Equal(g14,g17)
    c: Equal(g17,g4)
    c: Equal(g4,g9)
    c: DistanceX(g13,g13) = 6
    c: DistanceY(g19,g19) = 3.3
    c: DistanceX(g4,g12) = 4
    c: DistanceX(g14,g17) = 4
    c: Tangent(g22,g24) = -1.5708
    c: Tangent(g24,g23) = -1.5708
    c: Tangent(g23,g25) = -1.5708
    c: Tangent(g25,g22) = -1.5708
    c: Equal(g22,g23)
    c: PointOnObject(g22,g0)
    c: Tangent(g26,g28) = -1.5708
    c: Tangent(g28,g27) = -1.5708
    c: Tangent(g27,g29) = -1.5708
    c: Tangent(g29,g26) = -1.5708
    c: Equal(g26,g27)
    c: PointOnObject(g26,g0)
    c: Tangent(g30,g32) = -1.5708
    c: Tangent(g32,g31) = -1.5708
    c: Tangent(g31,g33) = -1.5708
    c: Tangent(g33,g30) = -1.5708
    c: Equal(g30,g31)
    c: PointOnObject(g30,g0)
    c: Tangent(g34,g36) = -1.5708
    c: Tangent(g36,g35) = -1.5708
    c: Tangent(g35,g37) = -1.5708
    c: Tangent(g37,g34) = -1.5708
    c: Equal(g34,g35)
    c: PointOnObject(g34,g0)
    c: Equal(g35,g23)
    c: Equal(g23,g27)
    c: Equal(g27,g31)
    c: Equal(g29,g33)
    c: Equal(g33,g25)
    c: Equal(g25,g37)
    c: Symmetric(g34,g35,g11)
    c: Symmetric(g22,g23,g6)
    c: Symmetric(g26,g27,g16)
    c: Symmetric(g30,g31,g21)
    c: Diameter(g31) = 3
    c: DistanceX(g33,g33) = 3
    c: DistanceY(g-1,g38) = 11.37
    c: Vertical(g38,g1)
    c: DistanceY(g23,g38) = 5.1
    c: DistanceY(g-1,g0) = 4.77
FEATURE [PartDesign::Pocket] Pocket010  label="TEK1_button"
  BaseFeature = -> Pocket008
  Direction = (0,0,-1)
  Length = 5
  Length2 = 5
  Profile = -> Sketch029
  ReferenceAxis = -> Sketch029 [N_Axis]
  Type = 0
FEATURE [TechDraw::DrawSVGTemplate] Template002
  Height = 210
  Orientation = 1
  Template = C:/Program Files/FreeCAD 0.21/data/Mod/TechDraw/Templates/A4_Landscape_blank.svg
  Width = 297
FEATURE [TechDraw::DrawViewAnnotation] Annotation002
  Font = osifont
  LineSpace = 100
  LockPosition = false
  MaxWidth = -1
  Rotation = 0
  ScaleType = 0
  Text = The mid of the datum plane A is preferred to be near | to the lower limit of the flatness tolerance zone. | It can be achieved with an additional bending step. | Aesthetical surfaces colored red on the view | No scratches, burrs or any kind of damage allowed! | Functional surfaces colored blue on the view (all which perpendicular to the aesthetical) | No burrs or other protruding material allowed!
  TextSize = 3
  TextStyle = 0
  X = 98.0147
  Y = 45.9809
FEATURE [Sketcher::SketchObject] Sketch030  label="TEK2_ButtonHole001"
  FullyConstrained = true
  MapMode = 5
  Support = -> [XY_Plane011]
  sketch-geometry (96):
    g0: Circle CenterX=-40.005 CenterY=-13.335 CenterZ=0 NormalX=0 NormalY=0 NormalZ=1 AngleXU=0 Radius=2
    g1: Circle CenterX=-13.335 CenterY=-13.335 CenterZ=0 NormalX=0 NormalY=0 NormalZ=1 AngleXU=0 Radius=2
    g2: LineSegment StartX=-40.005 StartY=-13.335 StartZ=0 EndX=-13.335 EndY=-13.335 EndZ=0
    g3: Circle CenterX=13.335 CenterY=-13.335 CenterZ=0 NormalX=0 NormalY=0 NormalZ=1 AngleXU=0 Radius=2
    g4: LineSegment StartX=-13.335 StartY=-13.335 StartZ=0 EndX=13.335 EndY=-13.335 EndZ=0
    g5: Circle CenterX=40.005 CenterY=-13.335 CenterZ=0 NormalX=0 NormalY=0 NormalZ=1 AngleXU=0 Radius=2
    g6: LineSegment StartX=13.335 StartY=-13.335 StartZ=0 EndX=40.005 EndY=-13.335 EndZ=0
    g7: Circle CenterX=-40.005 CenterY=-40.005 CenterZ=0 NormalX=0 NormalY=0 NormalZ=1 AngleXU=0 Radius=2
    g8: LineSegment StartX=-40.005 StartY=-13.335 StartZ=0 EndX=-40.005 EndY=-40.005 EndZ=0
    g9: Circle CenterX=-13.335 CenterY=-40.005 CenterZ=0 NormalX=0 NormalY=0 NormalZ=1 AngleXU=0 Radius=2
    g10: LineSegment StartX=-40.005 StartY=-40.005 StartZ=0 EndX=-13.335 EndY=-40.005 EndZ=0
    g11: Circle CenterX=13.335 CenterY=-40.005 CenterZ=0 NormalX=0 NormalY=0 NormalZ=1 AngleXU=0 Radius=2
    g12: LineSegment StartX=-13.335 StartY=-40.005 StartZ=0 EndX=13.335 EndY=-40.005 EndZ=0
    g13: Circle CenterX=40.005 CenterY=-40.005 CenterZ=0 NormalX=0 NormalY=0 NormalZ=1 AngleXU=0 Radius=2
    g14: LineSegment StartX=13.335 StartY=-40.005 StartZ=0 EndX=40.005 EndY=-40.005 EndZ=0
    g15: LineSegment StartX=0 StartY=0 StartZ=0 EndX=13.335 EndY=-13.335 EndZ=0
    g16: LineSegment StartX=0 StartY=0 StartZ=0 EndX=-13.335 EndY=-13.335 EndZ=0
    g17: LineSegment StartX=-48.505 StartY=-19.735 StartZ=0 EndX=-48.505 EndY=-6.935 EndZ=0
    g18: LineSegment StartX=-46.405 StartY=-4.835 StartZ=0 EndX=-33.605 EndY=-4.835 EndZ=0
    g19: LineSegment StartX=-31.505 StartY=-6.935 StartZ=0 EndX=-31.505 EndY=-19.735 EndZ=0
    g20: LineSegment StartX=-33.605 StartY=-21.835 StartZ=0 EndX=-46.405 EndY=-21.835 EndZ=0
    g21: GeomPoint X=-40.005 Y=-13.335 Z=0
    g22: LineSegment StartX=-21.835 StartY=-19.735 StartZ=0 EndX=-21.835 EndY=-6.935 EndZ=0
    g23: LineSegment StartX=-19.735 StartY=-4.835 StartZ=0 EndX=-6.935 EndY=-4.835 EndZ=0
    g24: LineSegment StartX=-4.835 StartY=-6.935 StartZ=0 EndX=-4.835 EndY=-19.735 EndZ=0
    g25: LineSegment StartX=-6.935 StartY=-21.835 StartZ=0 EndX=-19.735 EndY=-21.835 EndZ=0
    g26: GeomPoint X=-13.335 Y=-13.335 Z=0
    g27: LineSegment StartX=4.835 StartY=-19.735 StartZ=0 EndX=4.835 EndY=-6.935 EndZ=0
    g28: LineSegment StartX=6.935 StartY=-4.835 StartZ=0 EndX=19.735 EndY=-4.835 EndZ=0
    g29: LineSegment StartX=21.835 StartY=-6.935 StartZ=0 EndX=21.835 EndY=-19.735 EndZ=0
    g30: LineSegment StartX=19.735 StartY=-21.835 StartZ=0 EndX=6.935 EndY=-21.835 EndZ=0
    g31: GeomPoint X=13.335 Y=-13.335 Z=0
    g32: LineSegment StartX=31.505 StartY=-19.735 StartZ=0 EndX=31.505 EndY=-6.935 EndZ=0
    g33: LineSegment StartX=33.605 StartY=-4.835 StartZ=0 EndX=46.405 EndY=-4.835 EndZ=0
    g34: LineSegment StartX=48.505 StartY=-6.935 StartZ=0 EndX=48.505 EndY=-19.735 EndZ=0
    g35: LineSegment StartX=46.405 StartY=-21.835 StartZ=0 EndX=33.605 EndY=-21.835 EndZ=0
    g36: GeomPoint X=40.005 Y=-13.335 Z=0
    g37: LineSegment StartX=31.505 StartY=-46.405 StartZ=0 EndX=31.505 EndY=-33.605 EndZ=0
    g38: LineSegment StartX=33.605 StartY=-31.505 StartZ=0 EndX=46.405 EndY=-31.505 EndZ=0
    g39: LineSegment StartX=48.505 StartY=-33.605 StartZ=0 EndX=48.505 EndY=-46.405 EndZ=0
    g40: LineSegment StartX=46.405 StartY=-48.505 StartZ=0 EndX=33.605 EndY=-48.505 EndZ=0
    g41: GeomPoint X=40.005 Y=-40.005 Z=0
    g42: LineSegment StartX=4.835 StartY=-46.405 StartZ=0 EndX=4.835 EndY=-33.605 EndZ=0
    g43: LineSegment StartX=6.935 StartY=-31.505 StartZ=0 EndX=19.735 EndY=-31.505 EndZ=0
    g44: LineSegment StartX=21.835 StartY=-33.605 StartZ=0 EndX=21.835 EndY=-46.405 EndZ=0
    g45: LineSegment StartX=19.735 StartY=-48.505 StartZ=0 EndX=6.935 EndY=-48.505 EndZ=0
    g46: GeomPoint X=13.335 Y=-40.005 Z=0
    g47: LineSegment StartX=-21.835 StartY=-46.405 StartZ=0 EndX=-21.835 EndY=-33.605 EndZ=0
    g48: LineSegment StartX=-19.735 StartY=-31.505 StartZ=0 EndX=-6.935 EndY=-31.505 EndZ=0
    g49: LineSegment StartX=-4.835 StartY=-33.605 StartZ=0 EndX=-4.835 EndY=-46.405 EndZ=0
    g50: LineSegment StartX=-6.935 StartY=-48.505 StartZ=0 EndX=-19.735 EndY=-48.505 EndZ=0
    g51: GeomPoint X=-13.335 Y=-40.005 Z=0
    g52: LineSegment StartX=-48.505 StartY=-46.405 StartZ=0 EndX=-48.505 EndY=-33.605 EndZ=0
    g53: LineSegment StartX=-46.405 StartY=-31.505 StartZ=0 EndX=-33.605 EndY=-31.505 EndZ=0
    g54: LineSegment StartX=-31.505 StartY=-33.605 StartZ=0 EndX=-31.505 EndY=-46.405 EndZ=0
    g55: LineSegment StartX=-33.605 StartY=-48.505 StartZ=0 EndX=-46.405 EndY=-48.505 EndZ=0
    g56: GeomPoint X=-40.005 Y=-40.005 Z=0
    g57: ArcOfCircle CenterX=-46.405 CenterY=-6.935 CenterZ=0 NormalX=0 NormalY=0 NormalZ=1 AngleXU=0 Radius=2.1 StartAngle=1.5708 EndAngle=3.14159
    g58: ArcOfCircle CenterX=-46.405 CenterY=-19.735 CenterZ=0 NormalX=0 NormalY=0 NormalZ=1 AngleXU=0 Radius=2.1 StartAngle=3.14159 EndAngle=4.71239
    g59: ArcOfCircle CenterX=-33.605 CenterY=-19.735 CenterZ=0 NormalX=0 NormalY=0 NormalZ=1 AngleXU=0 Radius=2.1 StartAngle=4.71239 EndAngle=6.28319
    g60: ArcOfCircle CenterX=-33.605 CenterY=-6.935 CenterZ=0 NormalX=0 NormalY=0 NormalZ=1 AngleXU=0 Radius=2.1 StartAngle=0 EndAngle=1.5708
    g61: ArcOfCircle CenterX=-19.735 CenterY=-6.935 CenterZ=0 NormalX=0 NormalY=0 NormalZ=1 AngleXU=0 Radius=2.1 StartAngle=1.5708 EndAngle=3.14159
    g62: ArcOfCircle CenterX=-19.735 CenterY=-19.735 CenterZ=0 NormalX=0 NormalY=0 NormalZ=1 AngleXU=0 Radius=2.1 StartAngle=3.14159 EndAngle=4.71239
    g63: ArcOfCircle CenterX=-6.935 CenterY=-19.735 CenterZ=0 NormalX=0 NormalY=0 NormalZ=1 AngleXU=0 Radius=2.1 StartAngle=4.71239 EndAngle=6.28319
    g64: ArcOfCircle CenterX=-6.935 CenterY=-6.935 CenterZ=0 NormalX=0 NormalY=0 NormalZ=1 AngleXU=0 Radius=2.1 StartAngle=0 EndAngle=1.5708
    g65: ArcOfCircle CenterX=6.935 CenterY=-6.935 CenterZ=0 NormalX=0 NormalY=0 NormalZ=1 AngleXU=0 Radius=2.1 StartAngle=1.5708 EndAngle=3.14159
    g66: ArcOfCircle CenterX=19.735 CenterY=-6.935 CenterZ=0 NormalX=0 NormalY=0 NormalZ=1 AngleXU=0 Radius=2.1 StartAngle=0 EndAngle=1.5708
    g67: ArcOfCircle CenterX=19.735 CenterY=-19.735 CenterZ=0 NormalX=0 NormalY=0 NormalZ=1 AngleXU=0 Radius=2.1 StartAngle=4.71239 EndAngle=6.28319
    g68: ArcOfCircle CenterX=6.935 CenterY=-19.735 CenterZ=0 NormalX=0 NormalY=0 NormalZ=1 AngleXU=0 Radius=2.1 StartAngle=3.14159 EndAngle=4.71239
    g69: ArcOfCircle CenterX=33.605 CenterY=-6.935 CenterZ=0 NormalX=0 NormalY=0 NormalZ=1 AngleXU=0 Radius=2.1 StartAngle=1.5708 EndAngle=3.14159
    g70: ArcOfCircle CenterX=46.405 CenterY=-6.935 CenterZ=0 NormalX=0 NormalY=0 NormalZ=1 AngleXU=0 Radius=2.1 StartAngle=0 EndAngle=1.5708
    g71: ArcOfCircle CenterX=33.605 CenterY=-19.735 CenterZ=0 NormalX=0 NormalY=0 NormalZ=1 AngleXU=0 Radius=2.1 StartAngle=3.14159 EndAngle=4.71239
    g72: ArcOfCircle CenterX=46.405 CenterY=-19.735 CenterZ=0 NormalX=0 NormalY=0 NormalZ=1 AngleXU=0 Radius=2.1 StartAngle=4.71239 EndAngle=6.28319
    g73: ArcOfCircle CenterX=33.605 CenterY=-33.605 CenterZ=0 NormalX=0 NormalY=0 NormalZ=1 AngleXU=0 Radius=2.1 StartAngle=1.5708 EndAngle=3.14159
    g74: ArcOfCircle CenterX=46.405 CenterY=-33.605 CenterZ=0 NormalX=0 NormalY=0 NormalZ=1 AngleXU=0 Radius=2.1 StartAngle=-9e-16 EndAngle=1.5708
    g75: ArcOfCircle CenterX=46.405 CenterY=-46.405 CenterZ=0 NormalX=0 NormalY=0 NormalZ=1 AngleXU=0 Radius=2.1 StartAngle=4.71239 EndAngle=6.28319
    g76: ArcOfCircle CenterX=33.605 CenterY=-46.405 CenterZ=0 NormalX=0 NormalY=0 NormalZ=1 AngleXU=0 Radius=2.1 StartAngle=3.14159 EndAngle=4.71239
    g77: ArcOfCircle CenterX=6.935 CenterY=-33.605 CenterZ=0 NormalX=0 NormalY=0 NormalZ=1 AngleXU=0 Radius=2.1 StartAngle=1.5708 EndAngle=3.14159
    g78: ArcOfCircle CenterX=19.735 CenterY=-33.605 CenterZ=0 NormalX=0 NormalY=0 NormalZ=1 AngleXU=0 Radius=2.1 StartAngle=-9e-16 EndAngle=1.5708
    g79: ArcOfCircle CenterX=19.735 CenterY=-46.405 CenterZ=0 NormalX=0 NormalY=0 NormalZ=1 AngleXU=0 Radius=2.1 StartAngle=4.71239 EndAngle=6.28319
    g80: ArcOfCircle CenterX=6.935 CenterY=-46.405 CenterZ=0 NormalX=0 NormalY=0 NormalZ=1 AngleXU=0 Radius=2.1 StartAngle=3.14159 EndAngle=4.71239
    g81: ArcOfCircle CenterX=-19.735 CenterY=-33.605 CenterZ=0 NormalX=0 NormalY=0 NormalZ=1 AngleXU=0 Radius=2.1 StartAngle=1.5708 EndAngle=3.14159
    g82: ArcOfCircle CenterX=-6.935 CenterY=-33.605 CenterZ=0 NormalX=0 NormalY=0 NormalZ=1 AngleXU=0 Radius=2.1 StartAngle=1.6e-15 EndAngle=1.5708
    g83: ArcOfCircle CenterX=-6.935 CenterY=-46.405 CenterZ=0 NormalX=0 NormalY=0 NormalZ=1 AngleXU=0 Radius=2.1 StartAngle=4.71239 EndAngle=6.28319
    g84: ArcOfCircle CenterX=-19.735 CenterY=-46.405 CenterZ=0 NormalX=0 NormalY=0 NormalZ=1 AngleXU=0 Radius=2.1 StartAngle=3.14159 EndAngle=4.71239
    g85: ArcOfCircle CenterX=-46.405 CenterY=-33.605 CenterZ=0 NormalX=0 NormalY=0 NormalZ=1 AngleXU=0 Radius=2.1 StartAngle=1.5708 EndAngle=3.14159
    g86: ArcOfCircle CenterX=-33.605 CenterY=-33.605 CenterZ=0 NormalX=0 NormalY=0 NormalZ=1 AngleXU=0 Radius=2.1 StartAngle=-9e-16 EndAngle=1.5708
    g87: ArcOfCircle CenterX=-33.605 CenterY=-46.405 CenterZ=0 NormalX=0 NormalY=0 NormalZ=1 AngleXU=0 Radius=2.1 StartAngle=4.71239 EndAngle=6.28319
    g88: ArcOfCircle CenterX=-46.405 CenterY=-46.405 CenterZ=0 NormalX=0 NormalY=0 NormalZ=1 AngleXU=0 Radius=2.1 StartAngle=3.14159 EndAngle=4.71239
    g89: LineSegment StartX=-13.335 StartY=-4.835 StartZ=0 EndX=-13.335 EndY=-21.835 EndZ=0
    g90: LineSegment StartX=13.335 StartY=-4.835 StartZ=0 EndX=13.335 EndY=-21.835 EndZ=0
    g91: LineSegment StartX=40.005 StartY=-4.835 StartZ=0 EndX=40.005 EndY=-21.835 EndZ=0
    g92: LineSegment StartX=40.005 StartY=-31.505 StartZ=0 EndX=40.005 EndY=-48.505 EndZ=0
    g93: LineSegment StartX=13.335 StartY=-31.505 StartZ=0 EndX=13.335 EndY=-48.505 EndZ=0
    g94: LineSegment StartX=-13.335 StartY=-31.505 StartZ=0 EndX=-13.335 EndY=-48.505 EndZ=0
    g95: LineSegment StartX=-40.005 StartY=-31.505 StartZ=0 EndX=-40.005 EndY=-48.505 EndZ=0
  constraints (222):
    c: Diameter(g0) = 4
    c: Coincident(g0,g2)
    c: Coincident(g1,g2)
    c: Coincident(g1,g4)
    c: Coincident(g3,g4)
    c: Coincident(g3,g6)
    c: Coincident(g5,g6)
    c: Coincident(g0,g8)
    c: Coincident(g7,g8)
    c: Coincident(g7,g10)
    c: Coincident(g9,g10)
    c: Coincident(g9,g12)
    c: Coincident(g11,g12)
    c: Coincident(g11,g14)
    c: Coincident(g13,g14)
    c: Coincident(g-1,g16)
    c: Coincident(g16,g1)
    c: Coincident(g15,g3)
    c: Horizontal(g4)
    c: Horizontal(g2)
    c: Horizontal(g6)
    c: Horizontal(g10)
    c: Horizontal(g12)
    c: Horizontal(g14)
    c: Vertical(g8)
    c: Equal(g8,g2)
    c: Equal(g2,g10)
    c: Equal(g10,g12)
    c: Equal(g12,g4)
    c: Equal(g4,g6)
    c: Equal(g6,g14)
    c: DistanceX(g4,g4) = 26.67
    c: Equal(g16,g15)
    c: Coincident(g15,g16)
    c: Perpendicular(g15,g16)
    c: Equal(g7,g9)
    c: Equal(g9,g11)
    c: Equal(g11,g13)
    c: Equal(g13,g5)
    c: Equal(g5,g3)
    c: Equal(g3,g1)
    c: Equal(g1,g0)
    c: Horizontal(g18)
    c: Vertical(g17)
    c: Coincident(g21,g0)
    c: Horizontal(g23)
    c: Horizontal(g25)
    c: Vertical(g22)
    c: Coincident(g26,g1)
    c: Horizontal(g28)
    c: Horizontal(g30)
    c: Vertical(g27)
    c: Vertical(g29)
    c: Coincident(g31,g3)
    c: Horizontal(g33)
    c: Horizontal(g35)
    c: Vertical(g32)
    c: Vertical(g34)
    c: Coincident(g36,g5)
    c: Horizontal(g38)
    c: Horizontal(g40)
    c: Vertical(g37)
    c: Vertical(g39)
    c: Coincident(g41,g13)
    c: Horizontal(g43)
    c: Horizontal(g45)
    c: Vertical(g42)
    c: Vertical(g44)
    c: Coincident(g46,g11)
    c: Horizontal(g48)
    c: Horizontal(g50)
    c: Vertical(g47)
    c: Vertical(g49)
    c: Coincident(g51,g9)
    c: Horizontal(g53)
    c: Horizontal(g55)
    c: Vertical(g52)
    c: Vertical(g54)
    c: Coincident(g56,g7)
    c: Tangent(g17,g57) = 1.5708
    c: Tangent(g18,g57) = 1.5708
    c: Tangent(g17,g58) = 1.5708
    c: Tangent(g20,g58) = 1.5708
    c: Tangent(g19,g59) = 1.5708
    c: Tangent(g20,g59) = 1.5708
    c: Tangent(g19,g60) = 1.5708
    c: Tangent(g18,g60) = 1.5708
    c: Tangent(g23,g61) = 1.5708
    c: Tangent(g22,g61) = 1.5708
    c: Tangent(g22,g62) = 1.5708
    c: Tangent(g25,g62) = 1.5708
    c: Tangent(g24,g63) = 1.5708
    c: Tangent(g25,g63) = 1.5708
    c: Tangent(g23,g64) = 1.5708
    c: Tangent(g24,g64) = 1.5708
    c: Tangent(g28,g65) = 1.5708
    c: Tangent(g27,g65) = 1.5708
    c: Tangent(g29,g66) = 1.5708
    c: Tangent(g28,g66) = 1.5708
    c: Tangent(g29,g67) = 1.5708
    c: Tangent(g30,g67) = 1.5708
    c: Tangent(g27,g68) = 1.5708
    c: Tangent(g30,g68) = 1.5708
    c: Tangent(g33,g69) = 1.5708
    c: Tangent(g32,g69) = 1.5708
    c: Tangent(g33,g70) = 1.5708
    c: Tangent(g34,g70) = 1.5708
    c: Tangent(g32,g71) = 1.5708
    c: Tangent(g35,g71) = 1.5708
    c: Tangent(g34,g72) = 1.5708
    c: Tangent(g35,g72) = 1.5708
    c: Tangent(g38,g73) = 1.5708
    c: Tangent(g37,g73) = 1.5708
    c: Tangent(g38,g74) = 1.5708
    c: Tangent(g39,g74) = 1.5708
    c: Tangent(g39,g75) = 1.5708
    c: Tangent(g40,g75) = 1.5708
    c: Tangent(g37,g76) = 1.5708
    c: Tangent(g40,g76) = 1.5708
    c: Tangent(g43,g77) = 1.5708
    c: Tangent(g42,g77) = 1.5708
    c: Tangent(g43,g78) = 1.5708
    c: Tangent(g44,g78) = 1.5708
    c: Tangent(g44,g79) = 1.5708
    c: Tangent(g45,g79) = 1.5708
    c: Tangent(g42,g80) = 1.5708
    c: Tangent(g45,g80) = 1.5708
    c: Tangent(g48,g81) = 1.5708
    c: Tangent(g47,g81) = 1.5708
    c: Tangent(g48,g82) = 1.5708
    c: Tangent(g49,g82) = 1.5708
    c: Tangent(g49,g83) = 1.5708
    c: Tangent(g50,g83) = 1.5708
    c: Tangent(g47,g84) = 1.5708
    c: Tangent(g50,g84) = 1.5708
    c: Tangent(g52,g85) = 1.5708
    c: Tangent(g53,g85) = 1.5708
    c: Tangent(g53,g86) = 1.5708
    c: Tangent(g54,g86) = 1.5708
    c: Tangent(g54,g87) = 1.5708
    c: Tangent(g55,g87) = 1.5708
    c: Tangent(g52,g88) = 1.5708
    c: Tangent(g55,g88) = 1.5708
    c: Equal(g57,g58)
    c: Equal(g58,g60)
    c: Equal(g60,g59)
    c: Equal(g59,g62)
    c: Equal(g62,g61)
    c: Equal(g61,g64)
    c: Equal(g64,g63)
    c: Equal(g63,g68)
    c: Equal(g68,g65)
    c: Equal(g65,g66)
    c: Equal(g66,g67)
    c: Equal(g67,g71)
    c: Equal(g71,g69)
    c: Equal(g69,g70)
    c: Equal(g70,g72)
    c: Equal(g72,g73)
    c: Equal(g73,g74)
    c: Equal(g74,g75)
    c: Equal(g75,g76)
    c: Equal(g76,g79)
    c: Equal(g79,g80)
    c: Equal(g80,g77)
    c: Equal(g77,g78)
    c: Equal(g78,g82)
    c: Equal(g82,g81)
    c: Equal(g81,g83)
    c: Equal(g83,g84)
    c: Equal(g84,g87)
    c: Equal(g87,g88)
    c: Equal(g88,g85)
    c: Equal(g85,g86)
    c: Diameter(g57) = 4.2
    c: Equal(g19,g20)
    c: Symmetric(g19,g19,g2)
    c: Symmetric(g20,g20,g8)
    c: Symmetric(g24,g24,g4)
    c: PointOnObject(g89,g25)
    c: Vertical(g89)
    c: PointOnObject(g90,g30)
    c: Vertical(g90)
    c: PointOnObject(g91,g35)
    c: Vertical(g91)
    c: PointOnObject(g93,g45)
    c: PointOnObject(g94,g50)
    c: Vertical(g94)
    c: PointOnObject(g95,g55)
    c: Vertical(g95)
    c: Symmetric(g23,g23,g89)
    c: PointOnObject(g1,g89)
    c: Symmetric(g28,g28,g90)
    c: Symmetric(g33,g33,g91)
    c: PointOnObject(g92,g40)
    c: Vertical(g92)
    c: Symmetric(g38,g38,g92)
    c: Vertical(g93)
    c: Symmetric(g43,g43,g93)
    c: Symmetric(g48,g48,g94)
    c: Symmetric(g53,g53,g95)
    c: Equal(g19,g25)
    c: Equal(g25,g24)
    c: Equal(g24,g30)
    c: Equal(g30,g29)
    c: Equal(g29,g35)
    c: Equal(g35,g34)
    c: Equal(g34,g40)
    c: Equal(g40,g39)
    c: Equal(g39,g45)
    c: Equal(g45,g44)
    c: Equal(g44,g54)
    c: Equal(g54,g55)
    c: Equal(g55,g49)
    c: Equal(g49,g50)
    c: Symmetric(g94,g94,g9)
    c: Symmetric(g95,g95,g7)
    c: Symmetric(g93,g93,g11)
    c: Symmetric(g92,g92,g13)
    c: Symmetric(g91,g91,g5)
    c: Symmetric(g90,g90,g3)
    c: DistanceY(g20,g18) = 17
FEATURE [PartDesign::Pocket] Pocket011  label="TEK1_Buttonhole"
  BaseFeature = -> Pocket010
  Direction = (0,0,-1)
  Length = 5
  Length2 = 5
  Profile = -> Sketch030
  ReferenceAxis = -> Sketch030 [N_Axis]
  Type = 1
FEATURE [PartDesign::Body] Body011  label="FRONTPANEL-SHEET-VSN1-R"
  BaseFeature = -> Body
  Group = -> [Clone009,Sketch023,Sketch024,Sketch025,Pocket007,Sketch026,Sketch027,Pocket008,Sketch028,Sketch029,Pocket010,Sketch030,Pocket011]
  Origin = -> Origin011
  Tip = -> Pocket011
FEATURE [TechDraw::DrawViewPart] View
  CoarseView = false
  Direction = (0,0,1)
  Focus = 100
  HardHidden = true
  IsoCount = 0
  IsoHidden = false
  IsoVisible = false
  LockPosition = false
  Perspective = false
  Rotation = 0
  ScaleType = 0
  ScrubCount = 0
  SeamHidden = false
  SeamVisible = true
  SmoothHidden = false
  SmoothVisible = true
  Source = -> [Body011]
  X = 99.7276
  XDirection = (1,0,0)
  Y = 192.152
FEATURE [TechDraw::DrawViewPart] View001
  CoarseView = false
  Direction = (-1,0,0)
  Focus = 100
  HardHidden = true
  IsoCount = 0
  IsoHidden = false
  IsoVisible = false
  LockPosition = false
  Perspective = false
  Rotation = 0
  ScaleType = 0
  ScrubCount = 0
  SeamHidden = false
  SeamVisible = true
  SmoothHidden = false
  SmoothVisible = true
  Source = -> [Body011]
  X = 195.789
  XDirection = (0,0,1)
  Y = 193.481
FEATURE [TechDraw::DrawViewBalloon] Balloon002
  BubbleShape = 6
  EndType = 0
  EndTypeScale = 1
  KinkLength = -0.1
  LockPosition = false
  OriginX = 0.5
  OriginY = 0
  Rotation = 0
  ScaleType = 0
  ShapeScale = 1
  SourceView = -> View001
  Text = ⏥|0.2
  TextWrapLen = -1
  X = 18.3609
  Y = 18.1136
FEATURE [TechDraw::DrawViewBalloon] Balloon003
  BubbleShape = 6
  EndType = 6
  EndTypeScale = 1
  KinkLength = -0.1
  LockPosition = false
  OriginX = 0.672888
  OriginY = 39.7383
  Rotation = 0
  ScaleType = 0
  ShapeScale = 1
  SourceView = -> View001
  Text = A
  TextWrapLen = -1
  X = 10.7916
  Y = 39.8457
FEATURE [TechDraw::DrawViewBalloon] Balloon008
  BubbleShape = 1
  EndType = 0
  EndTypeScale = 1
  KinkLength = -0.1
  LockPosition = false
  OriginX = -52.0652
  OriginY = 52.0652
  Rotation = 0
  ScaleType = 0
  ShapeScale = 1
  SourceView = -> View
  Text = 4× R0.38
  TextWrapLen = -1
  X = -75.4388
  Y = 68.3556
FEATURE [TechDraw::DrawComplexSection] ComplexSection  label="Section A - A"
  BaseView = -> View
  Caption = Section A-A
  CoarseView = false
  CutSurfaceDisplay = 2
  CuttingToolWireObject = -> Sketch026
  Direction = (1e-16,-1,0)
  FileGeomPattern = C:/Program Files/FreeCAD 0.21/data/Mod/TechDraw/PAT/FCPAT.pat
  FileHatchPattern = C:/Program Files/FreeCAD 0.21/data/Mod/TechDraw/Patterns/simple.svg
  Focus = 100
  FuseBeforeCut = false
  HardHidden = true
  HatchOffset = (0,0,0)
  HatchRotation = 0
  HatchScale = 1
  IsoCount = 0
  IsoHidden = false
  IsoVisible = false
  LockPosition = false
  NameGeomPattern = Gyémánt bevonatú
  Perspective = false
  ProjectionStrategy = 1
  Rotation = 0
  Scale = 10
  ScaleType = 2
  ScrubCount = 0
  SeamHidden = false
  SeamVisible = true
  SectionDirection = 4
  SectionNormal = (1e-16,-1,0)
  SectionOrigin = (0,0,0)
  SectionSymbol = A
  SmoothHidden = false
  SmoothVisible = true
  Source = -> [Body011]
  TrimAfterCut = false
  X = 299.75
  XDirection = (1,1e-16,0)
  Y = 101.794
FEATURE [TechDraw::DrawViewDimension] Dimension008
  AngleOverride = false
  Arbitrary = false
  ArbitraryTolerances = false
  EqualTolerance = true
  ExtensionAngle = 0
  FormatSpec = 4x ⌀%.2w
  FormatSpecOverTolerance = %+.2w
  FormatSpecUnderTolerance = %+.2w
  Inverted = false
  LineAngle = 0
  LockPosition = false
  MeasureType = 1
  OverTolerance = 0
  References2D = -> [ComplexSection]
  Rotation = 0
  ScaleType = 0
  TheoreticalExact = false
  Type = 1
  UnderTolerance = 0
  X = 25.5096
  Y = 18.3127
FEATURE [TechDraw::DrawViewDimension] Dimension009
  AngleOverride = false
  Arbitrary = false
  ArbitraryTolerances = false
  EqualTolerance = true
  ExtensionAngle = 0
  FormatSpec = 4x ⌀%.2w
  FormatSpecOverTolerance = %+.2w
  FormatSpecUnderTolerance = %+.2w
  Inverted = false
  LineAngle = 0
  LockPosition = false
  MeasureType = 1
  OverTolerance = 0.05
  References2D = -> [ComplexSection]
  Rotation = 0
  ScaleType = 0
  TheoreticalExact = false
  Type = 1
  UnderTolerance = -0.05
  X = 48.7908
  Y = -4.80347
FEATURE [TechDraw::DrawViewBalloon] Balloon012
  BubbleShape = 6
  EndType = 6
  EndTypeScale = 1
  KinkLength = 0
  LockPosition = false
  OriginX = 46.1954
  OriginY = -17.0078
  Rotation = 0
  ScaleType = 0
  ShapeScale = 1
  SourceView = -> Dimension009
  Text = ⌖|⌀ 0.15|A|B|C
  TextWrapLen = -1
  X = 60.7039
  Y = -15.8876
FEATURE [TechDraw::DrawViewDimension] Dimension010
  AngleOverride = false
  Arbitrary = false
  ArbitraryTolerances = false
  EqualTolerance = true
  ExtensionAngle = 0
  FormatSpec = (%.2w)
  FormatSpecOverTolerance = %+.2w
  FormatSpecUnderTolerance = %+.2w
  Inverted = false
  LineAngle = 0
  LockPosition = false
  MeasureType = 1
  OverTolerance = 0
  References2D = -> [ComplexSection]
  Rotation = 0
  ScaleType = 0
  TheoreticalExact = false
  Type = 2
  UnderTolerance = 0
  X = -36.693
  Y = 2
FEATURE [TechDraw::DrawViewPart] View003
  CoarseView = false
  Direction = (0.57735,0.57735,0.57735)
  Focus = 100
  HardHidden = true
  IsoCount = 0
  IsoHidden = false
  IsoVisible = false
  LockPosition = false
  Perspective = false
  Rotation = 0
  Scale = 0.5
  ScaleType = 2
  ScrubCount = 0
  SeamHidden = false
  SeamVisible = true
  SmoothHidden = false
  SmoothVisible = true
  Source = -> [Body011]
  X = 195.17
  XDirection = (0.707107,0,-0.707107)
  Y = 86.0517
FEATURE [TechDraw::DrawHatch] Hatch  label="HatchF1"
  HatchPattern = C:/Program Files/FreeCAD 0.21/data/Mod/TechDraw/Patterns/solid.svg
  Source = -> View003 [Face1]
FEATURE [TechDraw::DrawViewBalloon] Balloon013
  BubbleShape = 1
  EndType = 3
  EndTypeScale = 1
  KinkLength = -0.1
  LockPosition = false
  OriginX = -18.2151
  OriginY = -14.1288
  Rotation = 0
  ScaleType = 0
  ShapeScale = 1
  SourceView = -> View003
  TextWrapLen = -1
  X = -124.961
  Y = -92.8185
FEATURE [TechDraw::DrawViewPart] View004
  CoarseView = false
  Direction = (0,0,1)
  Focus = 100
  HardHidden = false
  IsoCount = 0
  IsoHidden = false
  IsoVisible = true
  LockPosition = false
  Perspective = false
  Rotation = 0
  ScaleType = 0
  ScrubCount = 0
  SeamHidden = false
  SeamVisible = true
  SmoothHidden = false
  SmoothVisible = true
  Source = -> [Body011]
  X = 148.5
  XDirection = (1,3e-06,0)
  Y = 105
FEATURE [TechDraw::DrawPage] Page002  label="VSN1-R_dxf"
  KeepUpdated = true
  NextBalloonIndex = 1
  ProjectionType = 0
  Template = -> Template002
  Views = -> [View004]
FEATURE [TechDraw::DrawHatch] Hatch001  label="Hatch001F65"
  HatchPattern = C:/Program Files/FreeCAD 0.21/data/Mod/TechDraw/Patterns/solid.svg
  Source = -> View003 [Face5,Face4]
FEATURE [TechDraw::DrawViewDimension] Dimension019
  AngleOverride = false
  Arbitrary = false
  ArbitraryTolerances = false
  EqualTolerance = true
  ExtensionAngle = 0
  FormatSpec = %.2w
  FormatSpecOverTolerance = %+.2w
  FormatSpecUnderTolerance = %+.2w
  Inverted = false
  LineAngle = 0
  LockPosition = false
  MeasureType = 1
  OverTolerance = 0
  References2D = -> [ComplexSection]
  Rotation = 0
  ScaleType = 0
  TheoreticalExact = false
  Type = 6
  UnderTolerance = 0
  X = -23.1547
  Y = 24.2347
FEATURE [TechDraw::DrawViewDimension] Dimension
  AngleOverride = false
  Arbitrary = false
  ArbitraryTolerances = false
  EqualTolerance = true
  ExtensionAngle = 0
  FormatSpec = 4× 2×R%.2w
  FormatSpecOverTolerance = %+.2w
  FormatSpecUnderTolerance = %+.2w
  Inverted = false
  LineAngle = 0
  LockPosition = false
  MeasureType = 1
  OverTolerance = 0
  References2D = -> [View]
  Rotation = 0
  ScaleType = 0
  TheoreticalExact = false
  Type = 4
  UnderTolerance = 0
  X = 72.0302
  Y = -5.18053
FEATURE [TechDraw::DrawViewBalloon] Balloon023
  BubbleShape = 1
  EndType = 0
  EndTypeScale = 1
  KinkLength = 5
  LockPosition = false
  OriginX = 44.67
  OriginY = 4.77
  Rotation = 0
  ScaleType = 0
  ShapeScale = 1
  SourceView = -> View
  Text = 4× 3×6
  TextWrapLen = -1
  X = 70.083
  Y = -0.636336
FEATURE [TechDraw::DrawViewAnnotation] Annotation004
  Font = osifont
  LineSpace = 100
  LockPosition = false
  MaxWidth = -1
  Rotation = 0
  ScaleType = 0
  Text = 8x
  TextSize = 4
  TextStyle = 0
  X = 352.288
  Y = 191.609
FEATURE [TechDraw::DrawViewPart] View002
  CoarseView = false
  Direction = (0,0,-1)
  Focus = 100
  HardHidden = true
  IsoCount = 0
  IsoHidden = false
  IsoVisible = false
  LockPosition = false
  Perspective = false
  Rotation = 0
  ScaleType = 0
  ScrubCount = 0
  SeamHidden = false
  SeamVisible = true
  SmoothHidden = false
  SmoothVisible = true
  Source = -> [Body011]
  X = 287.327
  XDirection = (-1,0,0)
  Y = 189.984
FEATURE [TechDraw::DrawViewDimension] Dimension020
  AngleOverride = false
  Arbitrary = false
  ArbitraryTolerances = false
  EqualTolerance = true
  ExtensionAngle = 0
  FormatSpec = 8× %.2w
  FormatSpecOverTolerance = %+.2w
  FormatSpecUnderTolerance = %+.2w
  Inverted = false
  LineAngle = 0
  LockPosition = false
  MeasureType = 1
  OverTolerance = 0
  References2D = -> [View002]
  Rotation = 0
  ScaleType = 0
  TheoreticalExact = false
  Type = 2
  UnderTolerance = 0
  X = 56.7485
  Y = -37.8979
FEATURE [TechDraw::DrawViewDimension] Dimension021
  AngleOverride = false
  Arbitrary = false
  ArbitraryTolerances = false
  EqualTolerance = true
  ExtensionAngle = 0
  FormatSpec = 8× %.2w
  FormatSpecOverTolerance = %+.2w
  FormatSpecUnderTolerance = %+.2w
  Inverted = false
  LineAngle = 0
  LockPosition = false
  MeasureType = 1
  OverTolerance = 0
  References2D = -> [View002]
  Rotation = 0
  ScaleType = 0
  TheoreticalExact = false
  Type = 1
  UnderTolerance = 0
  X = 39.2555
  Y = -54.8555
FEATURE [TechDraw::DrawViewDimension] Dimension022
  AngleOverride = false
  Arbitrary = false
  ArbitraryTolerances = false
  EqualTolerance = true
  ExtensionAngle = 0
  FormatSpec = 8× 4×R%.2w
  FormatSpecOverTolerance = %+.2w
  FormatSpecUnderTolerance = %+.2w
  Inverted = false
  LineAngle = 0
  LockPosition = false
  MeasureType = 1
  OverTolerance = 0
  References2D = -> [View002]
  Rotation = 0
  ScaleType = 0
  TheoreticalExact = false
  Type = 4
  UnderTolerance = 0
  X = 71.9726
  Y = 11.9479
FEATURE [TechDraw::DrawViewBalloon] Balloon024
  BubbleShape = 6
  EndType = 0
  EndTypeScale = 1
  KinkLength = 5
  LockPosition = false
  OriginX = 47.7399
  OriginY = -21.0699
  Rotation = 0
  ScaleType = 0
  ShapeScale = 1
  SourceView = -> View002
  Text = ⌓|0.2|A|B|C
  TextWrapLen = -1
  X = 87.5108
  Y = -7.94379
FEATURE [TechDraw::DrawViewDimension] Dimension023
  AngleOverride = false
  Arbitrary = false
  ArbitraryTolerances = false
  EqualTolerance = true
  ExtensionAngle = 0
  FormatSpec = 5× ⌀%.2w
  FormatSpecOverTolerance = %+.2w
  FormatSpecUnderTolerance = %+.2w
  Inverted = false
  LineAngle = 0
  LockPosition = false
  MeasureType = 1
  OverTolerance = 0.05
  References2D = -> [View002]
  Rotation = 0
  ScaleType = 0
  TheoreticalExact = false
  Type = 5
  UnderTolerance = -0.05
  X = 76.0192
  Y = 56.5594
FEATURE [TechDraw::DrawViewDimension] Dimension024
  AngleOverride = false
  Arbitrary = false
  ArbitraryTolerances = false
  EqualTolerance = true
  ExtensionAngle = 0
  FormatSpec = (⌀%.2w)
  FormatSpecOverTolerance = %+.2w
  FormatSpecUnderTolerance = %+.2w
  Inverted = false
  LineAngle = 0
  LockPosition = false
  MeasureType = 1
  OverTolerance = 0
  References2D = -> [View]
  Rotation = 0
  ScaleType = 0
  TheoreticalExact = false
  Type = 5
  UnderTolerance = 0
  X = 0.602454
  Y = 86.7534
FEATURE [TechDraw::DrawViewBalloon] Balloon
  BubbleShape = 6
  EndType = 6
  EndTypeScale = 1
  KinkLength = 0
  LockPosition = false
  OriginX = 0.88228
  OriginY = 76.2418
  Rotation = 0
  ScaleType = 0
  ShapeScale = 1
  SourceView = -> Dimension024
  Text = ◎|⌀0.15|D
  TextWrapLen = -1
  X = 13.3086
  Y = 75.6668
FEATURE [TechDraw::DrawViewDimension] Dimension025
  AngleOverride = false
  Arbitrary = false
  ArbitraryTolerances = false
  EqualTolerance = true
  ExtensionAngle = 0
  FormatSpec = ⌀%.2w
  FormatSpecOverTolerance = %+.2w
  FormatSpecUnderTolerance = %+.2w
  Inverted = false
  LineAngle = 0
  LockPosition = false
  MeasureType = 1
  OverTolerance = 0
  References2D = -> [View002]
  Rotation = 0
  ScaleType = 0
  TheoreticalExact = false
  Type = 1
  UnderTolerance = 0
  X = 41.6878
  Y = 87.7591
FEATURE [TechDraw::DrawViewBalloon] Balloon025
  BubbleShape = 6
  EndType = 6
  EndTypeScale = 1
  KinkLength = 0
  LockPosition = false
  OriginX = 39.2104
  OriginY = 78.1934
  Rotation = 0
  ScaleType = 0
  ShapeScale = 1
  SourceView = -> Dimension025
  Text = ⌖|⌀0.15|A|B|C
  TextWrapLen = -1
  X = 65.2997
  Y = 76.665
FEATURE [TechDraw::DrawViewDimension] Dimension026
  AngleOverride = false
  Arbitrary = false
  ArbitraryTolerances = false
  EqualTolerance = true
  ExtensionAngle = 0
  FormatSpec = %.2w
  FormatSpecOverTolerance = %+.2w
  FormatSpecUnderTolerance = %+.2w
  Inverted = false
  LineAngle = 0
  LockPosition = false
  MeasureType = 1
  OverTolerance = 0
  References2D = -> [View]
  Rotation = 0
  ScaleType = 0
  TheoreticalExact = false
  Type = 1
  UnderTolerance = 0
  X = 25.6954
  Y = 62.2627
FEATURE [TechDraw::DrawViewDimension] Dimension027
  AngleOverride = false
  Arbitrary = false
  ArbitraryTolerances = false
  EqualTolerance = true
  ExtensionAngle = 0
  FormatSpec = %.2w
  FormatSpecOverTolerance = %+.2w
  FormatSpecUnderTolerance = %+.2w
  Inverted = false
  LineAngle = 0
  LockPosition = false
  MeasureType = 1
  OverTolerance = 0
  References2D = -> [View]
  Rotation = 0
  ScaleType = 0
  TheoreticalExact = false
  Type = 2
  UnderTolerance = 0
  X = 64.3881
  Y = 28.67
FEATURE [TechDraw::DrawViewDimension] Dimension028
  AngleOverride = false
  Arbitrary = false
  ArbitraryTolerances = false
  EqualTolerance = true
  ExtensionAngle = 0
  FormatSpec = 4× R%.2w
  FormatSpecOverTolerance = %+.2w
  FormatSpecUnderTolerance = %+.2w
  Inverted = false
  LineAngle = 0
  LockPosition = false
  MeasureType = 1
  OverTolerance = 0
  References2D = -> [View]
  Rotation = 0
  ScaleType = 0
  TheoreticalExact = false
  Type = 4
  UnderTolerance = 0
  X = 66.4473
  Y = 64.3323
FEATURE [TechDraw::DrawViewBalloon] Balloon026
  BubbleShape = 6
  EndType = 0
  EndTypeScale = 1
  KinkLength = 5
  LockPosition = false
  OriginX = -48.5842
  OriginY = 43.4842
  Rotation = 0
  ScaleType = 0
  ShapeScale = 1
  SourceView = -> View002
  Text = ⌓|0,2|A|B|C
  TextWrapLen = -1
  X = -10.6064
  Y = 71.0631
FEATURE [TechDraw::DrawViewBalloon] Balloon027
  BubbleShape = 6
  EndType = 6
  EndTypeScale = 1
  KinkLength = 0
  LockPosition = false
  OriginX = 72.7904
  OriginY = 47.3529
  Rotation = 0
  ScaleType = 0
  ShapeScale = 1
  SourceView = -> Dimension023
  Text = ⌖|⌀0.15|A|B|C
  TextWrapLen = -1
  X = 89.1298
  Y = 45.4792
FEATURE [TechDraw::DrawViewDimension] Dimension029
  AngleOverride = false
  Arbitrary = false
  ArbitraryTolerances = true
  EqualTolerance = false
  ExtensionAngle = 0
  FormatSpec = %.2w
  FormatSpecOverTolerance = +0
  FormatSpecUnderTolerance = -0.2
  Inverted = false
  LineAngle = 0
  LockPosition = false
  MeasureType = 1
  OverTolerance = 0
  References2D = -> [View002]
  Rotation = 0
  ScaleType = 0
  TheoreticalExact = false
  Type = 2
  UnderTolerance = 0
  X = -68.3985
  Y = 1.43626
FEATURE [TechDraw::DrawViewDimension] Dimension030
  AngleOverride = false
  Arbitrary = false
  ArbitraryTolerances = true
  EqualTolerance = false
  ExtensionAngle = 0
  FormatSpec = %.2w
  FormatSpecOverTolerance = +0
  FormatSpecUnderTolerance = -0.2
  Inverted = false
  LineAngle = 0
  LockPosition = false
  MeasureType = 1
  OverTolerance = 0
  References2D = -> [View]
  Rotation = 0
  ScaleType = 0
  TheoreticalExact = false
  Type = 1
  UnderTolerance = 0
  X = -0.695541
  Y = -58.958
FEATURE [TechDraw::DrawHatch] Hatch004  label="Hatch004F60"
  HatchPattern = C:/Program Files/FreeCAD 0.21/data/Mod/TechDraw/Patterns/solid.svg
  Source = -> View003 [Face60,Face20,Face113,Face21,Face63,Face61,Face62]
FEATURE [TechDraw::DrawHatch] Hatch005  label="Hatch005F76"
  HatchPattern = C:/Program Files/FreeCAD 0.21/data/Mod/TechDraw/Patterns/solid.svg
  Source = -> View003 [Face76,Face74,Face73,Face72,Face75,Face30,Face112,Face25,Face77,Face24,Face111]
FEATURE [TechDraw::DrawHatch] Hatch006  label="Hatch006F118"
  HatchPattern = C:/Program Files/FreeCAD 0.21/data/Mod/TechDraw/Patterns/solid.svg
  Source = -> View003 [Face118,Face85,Face78,Face121,Face82,Face79,Face120,Face84,Face81,Face119,Face83,Face80]
FEATURE [TechDraw::DrawHatch] Hatch007  label="Hatch007F108"
  HatchPattern = C:/Program Files/FreeCAD 0.21/data/Mod/TechDraw/Patterns/solid.svg
  Source = -> View003 [Face108,Face40,Face69,Face39,Face96,Face104,Face34,Face67,Face37,Face101,Face97,Face33,Face71,Face43,Face105,Face36,Face98,Face64,Face103,Face45]
FEATURE [TechDraw::DrawHatch] Hatch008  label="Hatch008F46"
  HatchPattern = C:/Program Files/FreeCAD 0.21/data/Mod/TechDraw/Patterns/solid.svg
  Source = -> View003 [Face46,Face110,Face70,Face32,Face106,Face95,Face35,Face65,Face42,Face107,Face41,Face102,Face68,Face31,Face109,Face99,Face66,Face44,Face100,Face38]
FEATURE [TechDraw::DrawViewBalloon] Balloon028
  BubbleShape = 6
  EndType = 6
  EndTypeScale = 1
  KinkLength = 0
  LockPosition = false
  OriginX = 52.1567
  OriginY = -65.782
  Rotation = 0
  ScaleType = 0
  ShapeScale = 1
  SourceView = -> Dimension030
  Text = B
  TextWrapLen = -1
  X = 64.5143
  Y = -65.8206
FEATURE [TechDraw::DrawViewBalloon] Balloon029
  BubbleShape = 6
  EndType = 6
  EndTypeScale = 1
  KinkLength = -0.1
  LockPosition = false
  OriginX = -59.6614
  OriginY = 52.1802
  Rotation = 0
  ScaleType = 0
  ShapeScale = 1
  SourceView = -> Dimension029
  Text = C
  TextWrapLen = -1
  X = -59.9431
  Y = 63.7574
FEATURE [TechDraw::DrawPage] Page  label="VSN1-R_Drawing"
  KeepUpdated = true
  NextBalloonIndex = 44
  ProjectionType = 0
  Template = -> Template
  Views = -> [View,View001,View002,Balloon002,Balloon003,Balloon008,ComplexSection,Dimension008,Dimension009,Balloon012,Dimension010,Annotation,View003,Balloon013,Annotation001,Annotation002,Dimension019,Dimension,Balloon023,Dimension020,Dimension021,Dimension022,Balloon024,Annotation004,Dimension023,Dimension024,Balloon,Dimension025,Balloon025,Dimension026,Dimension027,Dimension028,Balloon026,Balloon027,+4 more]
FEATURE [TechDraw::DrawHatch] Hatch009  label="Hatch009F16"
  HatchPattern = C:/Program Files/FreeCAD 0.21/data/Mod/TechDraw/Patterns/solid.svg
  Source = -> View003 [Face16,Face15,Face18,Face14,Face17,Face13,Face19,Face12,Face3,Face23]
